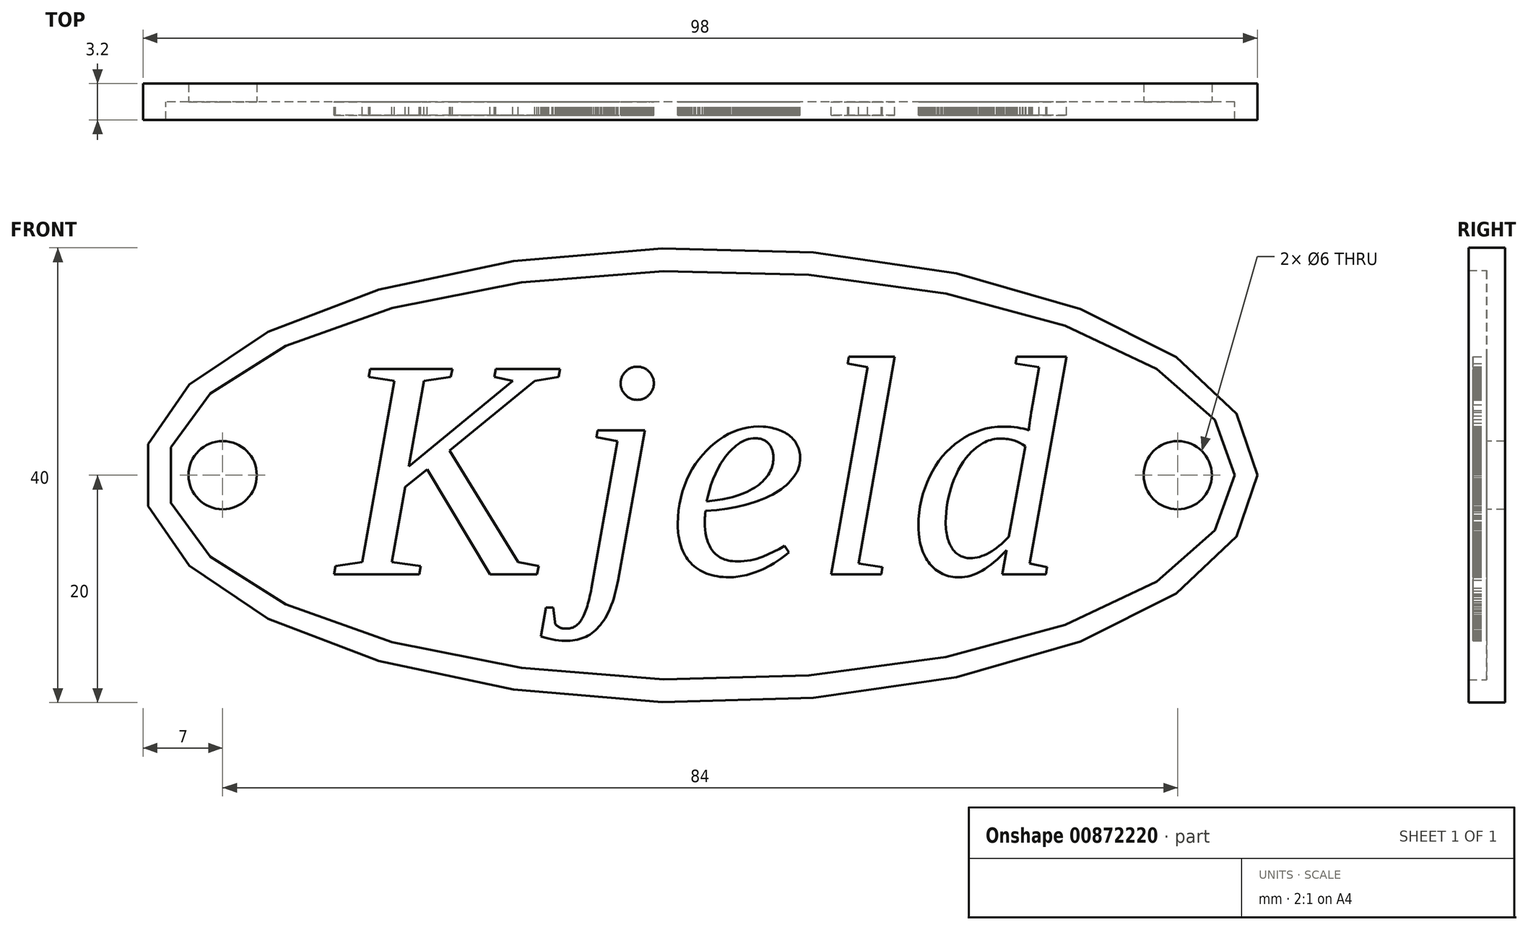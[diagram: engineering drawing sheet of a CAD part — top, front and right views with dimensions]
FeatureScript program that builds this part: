
annotation { "Feature Type Name" : "Feature", "Feature Type Description" : "" }
export const myFeature = defineFeature(function(context is Context, id is Id, definition is map)
    precondition{}
    {
        {
            var Q0;
            Q0=qCreatedBy(makeId("Front.planeOp"),FACE);
            var sketch = newSketch(context, id + "F0", { "sketchPlane" : qUnion([Q0])});
            skEllipse(sketch, "E0", {"center": v(0, 0) * mm, "majorRadius": 47 * mm, "minorRadius": 18 * mm, "majorAxis": v(1, 0)});
            skEllipse(sketch, "E1", {"center": v(0, 0) * mm, "majorRadius": 49 * mm, "minorRadius": 20 * mm, "majorAxis": v(1, 0)});
            skLineSegment(sketch, "E2", {"start": v(-81.12, 0) * mm, "end": v(85, 0) * mm, "construction": true});
            skPoint(sketch, "E2.startSnap0", {"position": v(-49, 0) * mm});
            skPoint(sketch, "E2.endSnap0", {"position": v(49, 0) * mm});
            skCircle(sketch, "E3", {"center": v(-42, 0) * mm, "radius": 3 * mm});
            skCircle(sketch, "E4", {"center": v(42, 0) * mm, "radius": 3 * mm});
            skLineSegment(sketch, "E5", {"start": v(-12.31, 9.35) * mm, "end": v(-12.45, 8.63) * mm});
            skLineSegment(sketch, "E6", {"start": v(-12.45, 8.63) * mm, "end": v(-14.55, 8.28) * mm});
            skLineSegment(sketch, "E7", {"start": v(-14.55, 8.28) * mm, "end": v(-22.03, 2.16) * mm});
            skLineSegment(sketch, "E8", {"start": v(-22.03, 2.16) * mm, "end": v(-16.02, -7.63) * mm});
            skLineSegment(sketch, "E9", {"start": v(-16.02, -7.63) * mm, "end": v(-14.21, -8) * mm});
            skLineSegment(sketch, "E10", {"start": v(-14.21, -8) * mm, "end": v(-14.35, -8.7) * mm});
            skLineSegment(sketch, "E11", {"start": v(-14.35, -8.7) * mm, "end": v(-18.48, -8.7) * mm});
            skLineSegment(sketch, "E12", {"start": v(-18.48, -8.7) * mm, "end": v(-24.01, 0.53) * mm});
            skLineSegment(sketch, "E13", {"start": v(-24.01, 0.53) * mm, "end": v(-25.94, -1.05) * mm});
            skLineSegment(sketch, "E14", {"start": v(-25.94, -1.05) * mm, "end": v(-27.12, -7.63) * mm});
            skLineSegment(sketch, "E15", {"start": v(-27.12, -7.63) * mm, "end": v(-24.6, -8) * mm});
            skLineSegment(sketch, "E16", {"start": v(-24.6, -8) * mm, "end": v(-24.73, -8.7) * mm});
            skLineSegment(sketch, "E17", {"start": v(-24.73, -8.7) * mm, "end": v(-32.21, -8.7) * mm});
            skLineSegment(sketch, "E18", {"start": v(-32.21, -8.7) * mm, "end": v(-32.08, -8) * mm});
            skLineSegment(sketch, "E19", {"start": v(-32.08, -8) * mm, "end": v(-29.72, -7.63) * mm});
            skLineSegment(sketch, "E20", {"start": v(-29.72, -7.63) * mm, "end": v(-26.9, 8.28) * mm});
            skLineSegment(sketch, "E21", {"start": v(-26.9, 8.28) * mm, "end": v(-29.17, 8.63) * mm});
            skLineSegment(sketch, "E22", {"start": v(-29.17, 8.63) * mm, "end": v(-29.03, 9.35) * mm});
            skLineSegment(sketch, "E23", {"start": v(-29.03, 9.35) * mm, "end": v(-21.8, 9.35) * mm});
            skLineSegment(sketch, "E24", {"start": v(-21.8, 9.35) * mm, "end": v(-21.94, 8.63) * mm});
            skLineSegment(sketch, "E25", {"start": v(-21.94, 8.63) * mm, "end": v(-24.3, 8.28) * mm});
            skLineSegment(sketch, "E26", {"start": v(-24.3, 8.28) * mm, "end": v(-25.63, 0.77) * mm});
            skLineSegment(sketch, "E27", {"start": v(-25.63, 0.77) * mm, "end": v(-16.5, 8.28) * mm});
            skLineSegment(sketch, "E28", {"start": v(-16.5, 8.28) * mm, "end": v(-18.1, 8.63) * mm});
            skLineSegment(sketch, "E29", {"start": v(-18.1, 8.63) * mm, "end": v(-17.97, 9.35) * mm});
            skLineSegment(sketch, "E30", {"start": v(-17.97, 9.35) * mm, "end": v(-12.31, 9.35) * mm});
            skLineSegment(sketch, "E31", {"start": v(-7.22, -9.23) * mm, "end": v(-7.36, -9.92) * mm});
            skLineSegment(sketch, "E32", {"start": v(-7.36, -9.92) * mm, "end": v(-7.52, -10.56) * mm});
            skLineSegment(sketch, "E33", {"start": v(-7.52, -10.56) * mm, "end": v(-7.61, -10.85) * mm});
            skLineSegment(sketch, "E34", {"start": v(-7.61, -10.85) * mm, "end": v(-7.7, -11.14) * mm});
            skLineSegment(sketch, "E35", {"start": v(-7.7, -11.14) * mm, "end": v(-7.8, -11.41) * mm});
            skLineSegment(sketch, "E36", {"start": v(-7.8, -11.41) * mm, "end": v(-7.9, -11.67) * mm});
            skLineSegment(sketch, "E37", {"start": v(-7.9, -11.67) * mm, "end": v(-8.02, -11.92) * mm});
            skLineSegment(sketch, "E38", {"start": v(-8.02, -11.92) * mm, "end": v(-8.13, -12.16) * mm});
            skLineSegment(sketch, "E39", {"start": v(-8.13, -12.16) * mm, "end": v(-8.25, -12.38) * mm});
            skLineSegment(sketch, "E40", {"start": v(-8.25, -12.38) * mm, "end": v(-8.37, -12.6) * mm});
            skLineSegment(sketch, "E41", {"start": v(-8.37, -12.6) * mm, "end": v(-8.5, -12.8) * mm});
            skLineSegment(sketch, "E42", {"start": v(-8.5, -12.8) * mm, "end": v(-8.63, -13) * mm});
            skLineSegment(sketch, "E43", {"start": v(-8.63, -13) * mm, "end": v(-8.77, -13.17) * mm});
            skLineSegment(sketch, "E44", {"start": v(-8.77, -13.17) * mm, "end": v(-8.92, -13.34) * mm});
            skLineSegment(sketch, "E45", {"start": v(-8.92, -13.34) * mm, "end": v(-9.07, -13.5) * mm});
            skLineSegment(sketch, "E46", {"start": v(-9.07, -13.5) * mm, "end": v(-9.22, -13.64) * mm});
            skLineSegment(sketch, "E47", {"start": v(-9.22, -13.64) * mm, "end": v(-9.38, -13.77) * mm});
            skLineSegment(sketch, "E48", {"start": v(-9.38, -13.77) * mm, "end": v(-9.54, -13.9) * mm});
            skLineSegment(sketch, "E49", {"start": v(-9.54, -13.9) * mm, "end": v(-9.7, -14.01) * mm});
            skLineSegment(sketch, "E50", {"start": v(-9.7, -14.01) * mm, "end": v(-9.88, -14.11) * mm});
            skLineSegment(sketch, "E51", {"start": v(-9.88, -14.11) * mm, "end": v(-10.06, -14.2) * mm});
            skLineSegment(sketch, "E52", {"start": v(-10.06, -14.2) * mm, "end": v(-10.24, -14.28) * mm});
            skLineSegment(sketch, "E53", {"start": v(-10.24, -14.28) * mm, "end": v(-10.43, -14.35) * mm});
            skLineSegment(sketch, "E54", {"start": v(-10.43, -14.35) * mm, "end": v(-10.62, -14.41) * mm});
            skLineSegment(sketch, "E55", {"start": v(-10.62, -14.41) * mm, "end": v(-10.81, -14.46) * mm});
            skLineSegment(sketch, "E56", {"start": v(-10.81, -14.46) * mm, "end": v(-11.01, -14.5) * mm});
            skLineSegment(sketch, "E57", {"start": v(-11.01, -14.5) * mm, "end": v(-11.22, -14.54) * mm});
            skLineSegment(sketch, "E58", {"start": v(-11.22, -14.54) * mm, "end": v(-11.43, -14.56) * mm});
            skLineSegment(sketch, "E59", {"start": v(-11.43, -14.56) * mm, "end": v(-11.64, -14.57) * mm});
            skLineSegment(sketch, "E60", {"start": v(-11.64, -14.57) * mm, "end": v(-11.85, -14.58) * mm});
            skLineSegment(sketch, "E61", {"start": v(-11.85, -14.58) * mm, "end": v(-12.16, -14.57) * mm});
            skLineSegment(sketch, "E62", {"start": v(-12.16, -14.57) * mm, "end": v(-12.45, -14.54) * mm});
            skLineSegment(sketch, "E63", {"start": v(-12.45, -14.54) * mm, "end": v(-12.75, -14.5) * mm});
            skLineSegment(sketch, "E64", {"start": v(-12.75, -14.5) * mm, "end": v(-13.04, -14.44) * mm});
            skLineSegment(sketch, "E65", {"start": v(-13.04, -14.44) * mm, "end": v(-13.32, -14.38) * mm});
            skLineSegment(sketch, "E66", {"start": v(-13.32, -14.38) * mm, "end": v(-13.45, -14.35) * mm});
            skLineSegment(sketch, "E67", {"start": v(-13.45, -14.35) * mm, "end": v(-13.57, -14.32) * mm});
            skLineSegment(sketch, "E68", {"start": v(-13.57, -14.32) * mm, "end": v(-13.69, -14.28) * mm});
            skLineSegment(sketch, "E69", {"start": v(-13.69, -14.28) * mm, "end": v(-13.8, -14.25) * mm});
            skLineSegment(sketch, "E70", {"start": v(-13.8, -14.25) * mm, "end": v(-13.9, -14.21) * mm});
            skLineSegment(sketch, "E71", {"start": v(-13.9, -14.21) * mm, "end": v(-14, -14.17) * mm});
            skLineSegment(sketch, "E72", {"start": v(-14, -14.17) * mm, "end": v(-13.56, -11.66) * mm});
            skLineSegment(sketch, "E73", {"start": v(-13.56, -11.66) * mm, "end": v(-12.93, -11.66) * mm});
            skLineSegment(sketch, "E74", {"start": v(-12.93, -11.66) * mm, "end": v(-12.73, -13.14) * mm});
            skLineSegment(sketch, "E75", {"start": v(-12.73, -13.14) * mm, "end": v(-12.7, -13.17) * mm});
            skLineSegment(sketch, "E76", {"start": v(-12.7, -13.17) * mm, "end": v(-12.65, -13.2) * mm});
            skLineSegment(sketch, "E77", {"start": v(-12.65, -13.2) * mm, "end": v(-12.6, -13.24) * mm});
            skLineSegment(sketch, "E78", {"start": v(-12.6, -13.24) * mm, "end": v(-12.56, -13.28) * mm});
            skLineSegment(sketch, "E79", {"start": v(-12.56, -13.28) * mm, "end": v(-12.51, -13.3) * mm});
            skLineSegment(sketch, "E80", {"start": v(-12.51, -13.3) * mm, "end": v(-12.46, -13.34) * mm});
            skLineSegment(sketch, "E81", {"start": v(-12.46, -13.34) * mm, "end": v(-12.4, -13.37) * mm});
            skLineSegment(sketch, "E82", {"start": v(-12.4, -13.37) * mm, "end": v(-12.35, -13.4) * mm});
            skLineSegment(sketch, "E83", {"start": v(-12.35, -13.4) * mm, "end": v(-12.3, -13.42) * mm});
            skLineSegment(sketch, "E84", {"start": v(-12.3, -13.42) * mm, "end": v(-12.23, -13.44) * mm});
            skLineSegment(sketch, "E85", {"start": v(-12.23, -13.44) * mm, "end": v(-12.16, -13.46) * mm});
            skLineSegment(sketch, "E86", {"start": v(-12.16, -13.46) * mm, "end": v(-12.1, -13.47) * mm});
            skLineSegment(sketch, "E87", {"start": v(-12.1, -13.47) * mm, "end": v(-12.02, -13.49) * mm});
            skLineSegment(sketch, "E88", {"start": v(-12.02, -13.49) * mm, "end": v(-11.94, -13.5) * mm});
            skLineSegment(sketch, "E89", {"start": v(-11.94, -13.5) * mm, "end": v(-11.86, -13.5) * mm});
            skLineSegment(sketch, "E90", {"start": v(-11.86, -13.5) * mm, "end": v(-11.77, -13.5) * mm});
            skLineSegment(sketch, "E91", {"start": v(-11.77, -13.5) * mm, "end": v(-11.68, -13.5) * mm});
            skLineSegment(sketch, "E92", {"start": v(-11.68, -13.5) * mm, "end": v(-11.59, -13.5) * mm});
            skLineSegment(sketch, "E93", {"start": v(-11.59, -13.5) * mm, "end": v(-11.5, -13.48) * mm});
            skLineSegment(sketch, "E94", {"start": v(-11.5, -13.48) * mm, "end": v(-11.41, -13.46) * mm});
            skLineSegment(sketch, "E95", {"start": v(-11.41, -13.46) * mm, "end": v(-11.32, -13.44) * mm});
            skLineSegment(sketch, "E96", {"start": v(-11.32, -13.44) * mm, "end": v(-11.24, -13.4) * mm});
            skLineSegment(sketch, "E97", {"start": v(-11.24, -13.4) * mm, "end": v(-11.16, -13.38) * mm});
            skLineSegment(sketch, "E98", {"start": v(-11.16, -13.38) * mm, "end": v(-11.07, -13.34) * mm});
            skLineSegment(sketch, "E99", {"start": v(-11.07, -13.34) * mm, "end": v(-11, -13.3) * mm});
            skLineSegment(sketch, "E100", {"start": v(-11, -13.3) * mm, "end": v(-10.92, -13.24) * mm});
            skLineSegment(sketch, "E101", {"start": v(-10.92, -13.24) * mm, "end": v(-10.84, -13.18) * mm});
            skLineSegment(sketch, "E102", {"start": v(-10.84, -13.18) * mm, "end": v(-10.76, -13.12) * mm});
            skLineSegment(sketch, "E103", {"start": v(-10.76, -13.12) * mm, "end": v(-10.7, -13.04) * mm});
            skLineSegment(sketch, "E104", {"start": v(-10.7, -13.04) * mm, "end": v(-10.62, -12.96) * mm});
            skLineSegment(sketch, "E105", {"start": v(-10.62, -12.96) * mm, "end": v(-10.55, -12.87) * mm});
            skLineSegment(sketch, "E106", {"start": v(-10.55, -12.87) * mm, "end": v(-10.48, -12.77) * mm});
            skLineSegment(sketch, "E107", {"start": v(-10.48, -12.77) * mm, "end": v(-10.41, -12.67) * mm});
            skLineSegment(sketch, "E108", {"start": v(-10.41, -12.67) * mm, "end": v(-10.35, -12.55) * mm});
            skLineSegment(sketch, "E109", {"start": v(-10.35, -12.55) * mm, "end": v(-10.29, -12.43) * mm});
            skLineSegment(sketch, "E110", {"start": v(-10.29, -12.43) * mm, "end": v(-10.22, -12.3) * mm});
            skLineSegment(sketch, "E111", {"start": v(-10.22, -12.3) * mm, "end": v(-10.16, -12.15) * mm});
            skLineSegment(sketch, "E112", {"start": v(-10.16, -12.15) * mm, "end": v(-10.1, -12) * mm});
            skLineSegment(sketch, "E113", {"start": v(-10.1, -12) * mm, "end": v(-10.04, -11.84) * mm});
            skLineSegment(sketch, "E114", {"start": v(-10.04, -11.84) * mm, "end": v(-9.98, -11.67) * mm});
            skLineSegment(sketch, "E115", {"start": v(-9.98, -11.67) * mm, "end": v(-9.93, -11.5) * mm});
            skLineSegment(sketch, "E116", {"start": v(-9.93, -11.5) * mm, "end": v(-9.87, -11.3) * mm});
            skLineSegment(sketch, "E117", {"start": v(-9.87, -11.3) * mm, "end": v(-9.82, -11.1) * mm});
            skLineSegment(sketch, "E118", {"start": v(-9.82, -11.1) * mm, "end": v(-9.76, -10.89) * mm});
            skLineSegment(sketch, "E119", {"start": v(-9.76, -10.89) * mm, "end": v(-9.71, -10.66) * mm});
            skLineSegment(sketch, "E120", {"start": v(-9.71, -10.66) * mm, "end": v(-9.66, -10.43) * mm});
            skLineSegment(sketch, "E121", {"start": v(-9.66, -10.43) * mm, "end": v(-9.61, -10.18) * mm});
            skLineSegment(sketch, "E122", {"start": v(-9.61, -10.18) * mm, "end": v(-9.57, -9.92) * mm});
            skLineSegment(sketch, "E123", {"start": v(-9.57, -9.92) * mm, "end": v(-7.28, 3) * mm});
            skLineSegment(sketch, "E124", {"start": v(-7.28, 3) * mm, "end": v(-9.12, 3.34) * mm});
            skLineSegment(sketch, "E125", {"start": v(-9.12, 3.34) * mm, "end": v(-9.01, 3.95) * mm});
            skLineSegment(sketch, "E126", {"start": v(-9.01, 3.95) * mm, "end": v(-4.88, 3.95) * mm});
            skLineSegment(sketch, "E127", {"start": v(-4.88, 3.95) * mm, "end": v(-7.22, -9.23) * mm});
            skLineSegment(sketch, "E128", {"start": v(-4.07, 8.08) * mm, "end": v(-4.07, 8) * mm});
            skLineSegment(sketch, "E129", {"start": v(-4.07, 8) * mm, "end": v(-4.08, 7.93) * mm});
            skLineSegment(sketch, "E130", {"start": v(-4.08, 7.93) * mm, "end": v(-4.1, 7.86) * mm});
            skLineSegment(sketch, "E131", {"start": v(-4.1, 7.86) * mm, "end": v(-4.1, 7.8) * mm});
            skLineSegment(sketch, "E132", {"start": v(-4.1, 7.8) * mm, "end": v(-4.12, 7.72) * mm});
            skLineSegment(sketch, "E133", {"start": v(-4.12, 7.72) * mm, "end": v(-4.14, 7.65) * mm});
            skLineSegment(sketch, "E134", {"start": v(-4.14, 7.65) * mm, "end": v(-4.17, 7.58) * mm});
            skLineSegment(sketch, "E135", {"start": v(-4.17, 7.58) * mm, "end": v(-4.2, 7.51) * mm});
            skLineSegment(sketch, "E136", {"start": v(-4.2, 7.51) * mm, "end": v(-4.22, 7.45) * mm});
            skLineSegment(sketch, "E137", {"start": v(-4.22, 7.45) * mm, "end": v(-4.25, 7.39) * mm});
            skLineSegment(sketch, "E138", {"start": v(-4.25, 7.39) * mm, "end": v(-4.29, 7.33) * mm});
            skLineSegment(sketch, "E139", {"start": v(-4.29, 7.33) * mm, "end": v(-4.33, 7.27) * mm});
            skLineSegment(sketch, "E140", {"start": v(-4.33, 7.27) * mm, "end": v(-4.37, 7.22) * mm});
            skLineSegment(sketch, "E141", {"start": v(-4.37, 7.22) * mm, "end": v(-4.4, 7.16) * mm});
            skLineSegment(sketch, "E142", {"start": v(-4.4, 7.16) * mm, "end": v(-4.45, 7.1) * mm});
            skLineSegment(sketch, "E143", {"start": v(-4.45, 7.1) * mm, "end": v(-4.5, 7.06) * mm});
            skLineSegment(sketch, "E144", {"start": v(-4.5, 7.06) * mm, "end": v(-4.56, 7) * mm});
            skLineSegment(sketch, "E145", {"start": v(-4.56, 7) * mm, "end": v(-4.6, 6.96) * mm});
            skLineSegment(sketch, "E146", {"start": v(-4.6, 6.96) * mm, "end": v(-4.66, 6.92) * mm});
            skLineSegment(sketch, "E147", {"start": v(-4.66, 6.92) * mm, "end": v(-4.72, 6.87) * mm});
            skLineSegment(sketch, "E148", {"start": v(-4.72, 6.87) * mm, "end": v(-4.78, 6.84) * mm});
            skLineSegment(sketch, "E149", {"start": v(-4.78, 6.84) * mm, "end": v(-4.84, 6.8) * mm});
            skLineSegment(sketch, "E150", {"start": v(-4.84, 6.8) * mm, "end": v(-4.9, 6.76) * mm});
            skLineSegment(sketch, "E151", {"start": v(-4.9, 6.76) * mm, "end": v(-4.98, 6.73) * mm});
            skLineSegment(sketch, "E152", {"start": v(-4.98, 6.73) * mm, "end": v(-5.04, 6.7) * mm});
            skLineSegment(sketch, "E153", {"start": v(-5.04, 6.7) * mm, "end": v(-5.11, 6.69) * mm});
            skLineSegment(sketch, "E154", {"start": v(-5.11, 6.69) * mm, "end": v(-5.18, 6.67) * mm});
            skLineSegment(sketch, "E155", {"start": v(-5.18, 6.67) * mm, "end": v(-5.25, 6.65) * mm});
            skLineSegment(sketch, "E156", {"start": v(-5.25, 6.65) * mm, "end": v(-5.32, 6.64) * mm});
            skLineSegment(sketch, "E157", {"start": v(-5.32, 6.64) * mm, "end": v(-5.4, 6.63) * mm});
            skLineSegment(sketch, "E158", {"start": v(-5.4, 6.63) * mm, "end": v(-5.47, 6.63) * mm});
            skLineSegment(sketch, "E159", {"start": v(-5.47, 6.63) * mm, "end": v(-5.54, 6.63) * mm});
            skLineSegment(sketch, "E160", {"start": v(-5.54, 6.63) * mm, "end": v(-5.61, 6.63) * mm});
            skLineSegment(sketch, "E161", {"start": v(-5.61, 6.63) * mm, "end": v(-5.69, 6.63) * mm});
            skLineSegment(sketch, "E162", {"start": v(-5.69, 6.63) * mm, "end": v(-5.76, 6.64) * mm});
            skLineSegment(sketch, "E163", {"start": v(-5.76, 6.64) * mm, "end": v(-5.83, 6.65) * mm});
            skLineSegment(sketch, "E164", {"start": v(-5.83, 6.65) * mm, "end": v(-5.9, 6.67) * mm});
            skLineSegment(sketch, "E165", {"start": v(-5.9, 6.67) * mm, "end": v(-5.97, 6.69) * mm});
            skLineSegment(sketch, "E166", {"start": v(-5.97, 6.69) * mm, "end": v(-6.04, 6.7) * mm});
            skLineSegment(sketch, "E167", {"start": v(-6.04, 6.7) * mm, "end": v(-6.1, 6.73) * mm});
            skLineSegment(sketch, "E168", {"start": v(-6.1, 6.73) * mm, "end": v(-6.23, 6.8) * mm});
            skLineSegment(sketch, "E169", {"start": v(-6.23, 6.8) * mm, "end": v(-6.35, 6.87) * mm});
            skLineSegment(sketch, "E170", {"start": v(-6.35, 6.87) * mm, "end": v(-6.46, 6.96) * mm});
            skLineSegment(sketch, "E171", {"start": v(-6.46, 6.96) * mm, "end": v(-6.56, 7.06) * mm});
            skLineSegment(sketch, "E172", {"start": v(-6.56, 7.06) * mm, "end": v(-6.66, 7.16) * mm});
            skLineSegment(sketch, "E173", {"start": v(-6.66, 7.16) * mm, "end": v(-6.75, 7.27) * mm});
            skLineSegment(sketch, "E174", {"start": v(-6.75, 7.27) * mm, "end": v(-6.82, 7.39) * mm});
            skLineSegment(sketch, "E175", {"start": v(-6.82, 7.39) * mm, "end": v(-6.89, 7.51) * mm});
            skLineSegment(sketch, "E176", {"start": v(-6.89, 7.51) * mm, "end": v(-6.91, 7.58) * mm});
            skLineSegment(sketch, "E177", {"start": v(-6.91, 7.58) * mm, "end": v(-6.93, 7.65) * mm});
            skLineSegment(sketch, "E178", {"start": v(-6.93, 7.65) * mm, "end": v(-6.95, 7.72) * mm});
            skLineSegment(sketch, "E179", {"start": v(-6.95, 7.72) * mm, "end": v(-6.97, 7.8) * mm});
            skLineSegment(sketch, "E180", {"start": v(-6.97, 7.8) * mm, "end": v(-6.98, 7.86) * mm});
            skLineSegment(sketch, "E181", {"start": v(-6.98, 7.86) * mm, "end": v(-6.99, 7.93) * mm});
            skLineSegment(sketch, "E182", {"start": v(-6.99, 7.93) * mm, "end": v(-7, 8) * mm});
            skLineSegment(sketch, "E183", {"start": v(-7, 8) * mm, "end": v(-7, 8.08) * mm});
            skLineSegment(sketch, "E184", {"start": v(-7, 8.08) * mm, "end": v(-7, 8.15) * mm});
            skLineSegment(sketch, "E185", {"start": v(-7, 8.15) * mm, "end": v(-6.99, 8.23) * mm});
            skLineSegment(sketch, "E186", {"start": v(-6.99, 8.23) * mm, "end": v(-6.98, 8.3) * mm});
            skLineSegment(sketch, "E187", {"start": v(-6.98, 8.3) * mm, "end": v(-6.97, 8.37) * mm});
            skLineSegment(sketch, "E188", {"start": v(-6.97, 8.37) * mm, "end": v(-6.95, 8.44) * mm});
            skLineSegment(sketch, "E189", {"start": v(-6.95, 8.44) * mm, "end": v(-6.93, 8.5) * mm});
            skLineSegment(sketch, "E190", {"start": v(-6.93, 8.5) * mm, "end": v(-6.91, 8.58) * mm});
            skLineSegment(sketch, "E191", {"start": v(-6.91, 8.58) * mm, "end": v(-6.89, 8.65) * mm});
            skLineSegment(sketch, "E192", {"start": v(-6.89, 8.65) * mm, "end": v(-6.86, 8.71) * mm});
            skLineSegment(sketch, "E193", {"start": v(-6.86, 8.71) * mm, "end": v(-6.82, 8.78) * mm});
            skLineSegment(sketch, "E194", {"start": v(-6.82, 8.78) * mm, "end": v(-6.78, 8.84) * mm});
            skLineSegment(sketch, "E195", {"start": v(-6.78, 8.84) * mm, "end": v(-6.75, 8.9) * mm});
            skLineSegment(sketch, "E196", {"start": v(-6.75, 8.9) * mm, "end": v(-6.7, 8.96) * mm});
            skLineSegment(sketch, "E197", {"start": v(-6.7, 8.96) * mm, "end": v(-6.66, 9.01) * mm});
            skLineSegment(sketch, "E198", {"start": v(-6.66, 9.01) * mm, "end": v(-6.61, 9.06) * mm});
            skLineSegment(sketch, "E199", {"start": v(-6.61, 9.06) * mm, "end": v(-6.56, 9.12) * mm});
            skLineSegment(sketch, "E200", {"start": v(-6.56, 9.12) * mm, "end": v(-6.51, 9.17) * mm});
            skLineSegment(sketch, "E201", {"start": v(-6.51, 9.17) * mm, "end": v(-6.46, 9.21) * mm});
            skLineSegment(sketch, "E202", {"start": v(-6.46, 9.21) * mm, "end": v(-6.4, 9.25) * mm});
            skLineSegment(sketch, "E203", {"start": v(-6.4, 9.25) * mm, "end": v(-6.35, 9.3) * mm});
            skLineSegment(sketch, "E204", {"start": v(-6.35, 9.3) * mm, "end": v(-6.3, 9.33) * mm});
            skLineSegment(sketch, "E205", {"start": v(-6.3, 9.33) * mm, "end": v(-6.23, 9.37) * mm});
            skLineSegment(sketch, "E206", {"start": v(-6.23, 9.37) * mm, "end": v(-6.17, 9.4) * mm});
            skLineSegment(sketch, "E207", {"start": v(-6.17, 9.4) * mm, "end": v(-6.1, 9.43) * mm});
            skLineSegment(sketch, "E208", {"start": v(-6.1, 9.43) * mm, "end": v(-6.04, 9.45) * mm});
            skLineSegment(sketch, "E209", {"start": v(-6.04, 9.45) * mm, "end": v(-5.97, 9.48) * mm});
            skLineSegment(sketch, "E210", {"start": v(-5.97, 9.48) * mm, "end": v(-5.9, 9.5) * mm});
            skLineSegment(sketch, "E211", {"start": v(-5.9, 9.5) * mm, "end": v(-5.83, 9.52) * mm});
            skLineSegment(sketch, "E212", {"start": v(-5.83, 9.52) * mm, "end": v(-5.76, 9.53) * mm});
            skLineSegment(sketch, "E213", {"start": v(-5.76, 9.53) * mm, "end": v(-5.69, 9.54) * mm});
            skLineSegment(sketch, "E214", {"start": v(-5.69, 9.54) * mm, "end": v(-5.61, 9.55) * mm});
            skLineSegment(sketch, "E215", {"start": v(-5.61, 9.55) * mm, "end": v(-5.54, 9.55) * mm});
            skLineSegment(sketch, "E216", {"start": v(-5.54, 9.55) * mm, "end": v(-5.47, 9.55) * mm});
            skLineSegment(sketch, "E217", {"start": v(-5.47, 9.55) * mm, "end": v(-5.4, 9.54) * mm});
            skLineSegment(sketch, "E218", {"start": v(-5.4, 9.54) * mm, "end": v(-5.32, 9.53) * mm});
            skLineSegment(sketch, "E219", {"start": v(-5.32, 9.53) * mm, "end": v(-5.25, 9.52) * mm});
            skLineSegment(sketch, "E220", {"start": v(-5.25, 9.52) * mm, "end": v(-5.18, 9.5) * mm});
            skLineSegment(sketch, "E221", {"start": v(-5.18, 9.5) * mm, "end": v(-5.11, 9.48) * mm});
            skLineSegment(sketch, "E222", {"start": v(-5.11, 9.48) * mm, "end": v(-5.04, 9.45) * mm});
            skLineSegment(sketch, "E223", {"start": v(-5.04, 9.45) * mm, "end": v(-4.98, 9.43) * mm});
            skLineSegment(sketch, "E224", {"start": v(-4.98, 9.43) * mm, "end": v(-4.9, 9.4) * mm});
            skLineSegment(sketch, "E225", {"start": v(-4.9, 9.4) * mm, "end": v(-4.84, 9.37) * mm});
            skLineSegment(sketch, "E226", {"start": v(-4.84, 9.37) * mm, "end": v(-4.78, 9.33) * mm});
            skLineSegment(sketch, "E227", {"start": v(-4.78, 9.33) * mm, "end": v(-4.72, 9.3) * mm});
            skLineSegment(sketch, "E228", {"start": v(-4.72, 9.3) * mm, "end": v(-4.66, 9.25) * mm});
            skLineSegment(sketch, "E229", {"start": v(-4.66, 9.25) * mm, "end": v(-4.6, 9.21) * mm});
            skLineSegment(sketch, "E230", {"start": v(-4.6, 9.21) * mm, "end": v(-4.56, 9.17) * mm});
            skLineSegment(sketch, "E231", {"start": v(-4.56, 9.17) * mm, "end": v(-4.5, 9.12) * mm});
            skLineSegment(sketch, "E232", {"start": v(-4.5, 9.12) * mm, "end": v(-4.45, 9.06) * mm});
            skLineSegment(sketch, "E233", {"start": v(-4.45, 9.06) * mm, "end": v(-4.4, 9.01) * mm});
            skLineSegment(sketch, "E234", {"start": v(-4.4, 9.01) * mm, "end": v(-4.37, 8.96) * mm});
            skLineSegment(sketch, "E235", {"start": v(-4.37, 8.96) * mm, "end": v(-4.33, 8.9) * mm});
            skLineSegment(sketch, "E236", {"start": v(-4.33, 8.9) * mm, "end": v(-4.29, 8.84) * mm});
            skLineSegment(sketch, "E237", {"start": v(-4.29, 8.84) * mm, "end": v(-4.25, 8.78) * mm});
            skLineSegment(sketch, "E238", {"start": v(-4.25, 8.78) * mm, "end": v(-4.22, 8.71) * mm});
            skLineSegment(sketch, "E239", {"start": v(-4.22, 8.71) * mm, "end": v(-4.2, 8.65) * mm});
            skLineSegment(sketch, "E240", {"start": v(-4.2, 8.65) * mm, "end": v(-4.17, 8.58) * mm});
            skLineSegment(sketch, "E241", {"start": v(-4.17, 8.58) * mm, "end": v(-4.14, 8.5) * mm});
            skLineSegment(sketch, "E242", {"start": v(-4.14, 8.5) * mm, "end": v(-4.12, 8.44) * mm});
            skLineSegment(sketch, "E243", {"start": v(-4.12, 8.44) * mm, "end": v(-4.1, 8.37) * mm});
            skLineSegment(sketch, "E244", {"start": v(-4.1, 8.37) * mm, "end": v(-4.1, 8.3) * mm});
            skLineSegment(sketch, "E245", {"start": v(-4.1, 8.3) * mm, "end": v(-4.08, 8.23) * mm});
            skLineSegment(sketch, "E246", {"start": v(-4.08, 8.23) * mm, "end": v(-4.07, 8.15) * mm});
            skLineSegment(sketch, "E247", {"start": v(-4.07, 8.15) * mm, "end": v(-4.07, 8.08) * mm});
            skLineSegment(sketch, "E248", {"start": v(8.8, 1.52) * mm, "end": v(8.79, 1.3) * mm});
            skLineSegment(sketch, "E249", {"start": v(8.79, 1.3) * mm, "end": v(8.76, 1.1) * mm});
            skLineSegment(sketch, "E250", {"start": v(8.76, 1.1) * mm, "end": v(8.72, 0.88) * mm});
            skLineSegment(sketch, "E251", {"start": v(8.72, 0.88) * mm, "end": v(8.66, 0.67) * mm});
            skLineSegment(sketch, "E252", {"start": v(8.66, 0.67) * mm, "end": v(8.58, 0.47) * mm});
            skLineSegment(sketch, "E253", {"start": v(8.58, 0.47) * mm, "end": v(8.49, 0.26) * mm});
            skLineSegment(sketch, "E254", {"start": v(8.49, 0.26) * mm, "end": v(8.38, 0.06) * mm});
            skLineSegment(sketch, "E255", {"start": v(8.38, 0.06) * mm, "end": v(8.25, -0.13) * mm});
            skLineSegment(sketch, "E256", {"start": v(8.25, -0.13) * mm, "end": v(8.1, -0.33) * mm});
            skLineSegment(sketch, "E257", {"start": v(8.1, -0.33) * mm, "end": v(7.94, -0.51) * mm});
            skLineSegment(sketch, "E258", {"start": v(7.94, -0.51) * mm, "end": v(7.76, -0.7) * mm});
            skLineSegment(sketch, "E259", {"start": v(7.76, -0.7) * mm, "end": v(7.57, -0.88) * mm});
            skLineSegment(sketch, "E260", {"start": v(7.57, -0.88) * mm, "end": v(7.36, -1.05) * mm});
            skLineSegment(sketch, "E261", {"start": v(7.36, -1.05) * mm, "end": v(7.13, -1.22) * mm});
            skLineSegment(sketch, "E262", {"start": v(7.13, -1.22) * mm, "end": v(6.89, -1.39) * mm});
            skLineSegment(sketch, "E263", {"start": v(6.89, -1.39) * mm, "end": v(6.63, -1.55) * mm});
            skLineSegment(sketch, "E264", {"start": v(6.63, -1.55) * mm, "end": v(6.36, -1.7) * mm});
            skLineSegment(sketch, "E265", {"start": v(6.36, -1.7) * mm, "end": v(6.07, -1.84) * mm});
            skLineSegment(sketch, "E266", {"start": v(6.07, -1.84) * mm, "end": v(5.77, -1.98) * mm});
            skLineSegment(sketch, "E267", {"start": v(5.77, -1.98) * mm, "end": v(5.45, -2.12) * mm});
            skLineSegment(sketch, "E268", {"start": v(5.45, -2.12) * mm, "end": v(5.12, -2.25) * mm});
            skLineSegment(sketch, "E269", {"start": v(5.12, -2.25) * mm, "end": v(4.77, -2.37) * mm});
            skLineSegment(sketch, "E270", {"start": v(4.77, -2.37) * mm, "end": v(4.02, -2.6) * mm});
            skLineSegment(sketch, "E271", {"start": v(4.02, -2.6) * mm, "end": v(3.22, -2.79) * mm});
            skLineSegment(sketch, "E272", {"start": v(3.22, -2.79) * mm, "end": v(2.36, -2.94) * mm});
            skLineSegment(sketch, "E273", {"start": v(2.36, -2.94) * mm, "end": v(1.44, -3.06) * mm});
            skLineSegment(sketch, "E274", {"start": v(1.44, -3.06) * mm, "end": v(0.46, -3.15) * mm});
            skLineSegment(sketch, "E275", {"start": v(0.46, -3.15) * mm, "end": v(0.46, -3.16) * mm});
            skLineSegment(sketch, "E276", {"start": v(0.46, -3.16) * mm, "end": v(0.46, -3.18) * mm});
            skLineSegment(sketch, "E277", {"start": v(0.46, -3.18) * mm, "end": v(0.46, -3.2) * mm});
            skLineSegment(sketch, "E278", {"start": v(0.46, -3.2) * mm, "end": v(0.46, -3.22) * mm});
            skLineSegment(sketch, "E279", {"start": v(0.46, -3.22) * mm, "end": v(0.45, -3.24) * mm});
            skLineSegment(sketch, "E280", {"start": v(0.45, -3.24) * mm, "end": v(0.45, -3.26) * mm});
            skLineSegment(sketch, "E281", {"start": v(0.45, -3.26) * mm, "end": v(0.45, -3.28) * mm});
            skLineSegment(sketch, "E282", {"start": v(0.45, -3.28) * mm, "end": v(0.45, -3.3) * mm});
            skLineSegment(sketch, "E283", {"start": v(0.45, -3.3) * mm, "end": v(0.44, -3.35) * mm});
            skLineSegment(sketch, "E284", {"start": v(0.44, -3.35) * mm, "end": v(0.44, -3.4) * mm});
            skLineSegment(sketch, "E285", {"start": v(0.44, -3.4) * mm, "end": v(0.43, -3.46) * mm});
            skLineSegment(sketch, "E286", {"start": v(0.43, -3.46) * mm, "end": v(0.42, -3.53) * mm});
            skLineSegment(sketch, "E287", {"start": v(0.42, -3.53) * mm, "end": v(0.42, -3.6) * mm});
            skLineSegment(sketch, "E288", {"start": v(0.42, -3.6) * mm, "end": v(0.42, -3.73) * mm});
            skLineSegment(sketch, "E289", {"start": v(0.42, -3.73) * mm, "end": v(0.41, -3.88) * mm});
            skLineSegment(sketch, "E290", {"start": v(0.41, -3.88) * mm, "end": v(0.41, -4.04) * mm});
            skLineSegment(sketch, "E291", {"start": v(0.41, -4.04) * mm, "end": v(0.41, -4.13) * mm});
            skLineSegment(sketch, "E292", {"start": v(0.41, -4.13) * mm, "end": v(0.42, -4.46) * mm});
            skLineSegment(sketch, "E293", {"start": v(0.42, -4.46) * mm, "end": v(0.44, -4.78) * mm});
            skLineSegment(sketch, "E294", {"start": v(0.44, -4.78) * mm, "end": v(0.48, -5.1) * mm});
            skLineSegment(sketch, "E295", {"start": v(0.48, -5.1) * mm, "end": v(0.53, -5.4) * mm});
            skLineSegment(sketch, "E296", {"start": v(0.53, -5.4) * mm, "end": v(0.57, -5.56) * mm});
            skLineSegment(sketch, "E297", {"start": v(0.57, -5.56) * mm, "end": v(0.61, -5.71) * mm});
            skLineSegment(sketch, "E298", {"start": v(0.61, -5.71) * mm, "end": v(0.66, -5.86) * mm});
            skLineSegment(sketch, "E299", {"start": v(0.66, -5.86) * mm, "end": v(0.71, -6) * mm});
            skLineSegment(sketch, "E300", {"start": v(0.71, -6) * mm, "end": v(0.77, -6.13) * mm});
            skLineSegment(sketch, "E301", {"start": v(0.77, -6.13) * mm, "end": v(0.84, -6.26) * mm});
            skLineSegment(sketch, "E302", {"start": v(0.84, -6.26) * mm, "end": v(0.91, -6.4) * mm});
            skLineSegment(sketch, "E303", {"start": v(0.91, -6.4) * mm, "end": v(0.99, -6.51) * mm});
            skLineSegment(sketch, "E304", {"start": v(0.99, -6.51) * mm, "end": v(1.07, -6.63) * mm});
            skLineSegment(sketch, "E305", {"start": v(1.07, -6.63) * mm, "end": v(1.17, -6.74) * mm});
            skLineSegment(sketch, "E306", {"start": v(1.17, -6.74) * mm, "end": v(1.26, -6.85) * mm});
            skLineSegment(sketch, "E307", {"start": v(1.26, -6.85) * mm, "end": v(1.37, -6.95) * mm});
            skLineSegment(sketch, "E308", {"start": v(1.37, -6.95) * mm, "end": v(1.48, -7.05) * mm});
            skLineSegment(sketch, "E309", {"start": v(1.48, -7.05) * mm, "end": v(1.6, -7.13) * mm});
            skLineSegment(sketch, "E310", {"start": v(1.6, -7.13) * mm, "end": v(1.73, -7.22) * mm});
            skLineSegment(sketch, "E311", {"start": v(1.73, -7.22) * mm, "end": v(1.86, -7.3) * mm});
            skLineSegment(sketch, "E312", {"start": v(1.86, -7.3) * mm, "end": v(2, -7.36) * mm});
            skLineSegment(sketch, "E313", {"start": v(2, -7.36) * mm, "end": v(2.16, -7.42) * mm});
            skLineSegment(sketch, "E314", {"start": v(2.16, -7.42) * mm, "end": v(2.32, -7.47) * mm});
            skLineSegment(sketch, "E315", {"start": v(2.32, -7.47) * mm, "end": v(2.5, -7.5) * mm});
            skLineSegment(sketch, "E316", {"start": v(2.5, -7.5) * mm, "end": v(2.67, -7.54) * mm});
            skLineSegment(sketch, "E317", {"start": v(2.67, -7.54) * mm, "end": v(2.86, -7.56) * mm});
            skLineSegment(sketch, "E318", {"start": v(2.86, -7.56) * mm, "end": v(3.06, -7.57) * mm});
            skLineSegment(sketch, "E319", {"start": v(3.06, -7.57) * mm, "end": v(3.26, -7.58) * mm});
            skLineSegment(sketch, "E320", {"start": v(3.26, -7.58) * mm, "end": v(3.56, -7.57) * mm});
            skLineSegment(sketch, "E321", {"start": v(3.56, -7.57) * mm, "end": v(3.86, -7.55) * mm});
            skLineSegment(sketch, "E322", {"start": v(3.86, -7.55) * mm, "end": v(4.15, -7.52) * mm});
            skLineSegment(sketch, "E323", {"start": v(4.15, -7.52) * mm, "end": v(4.43, -7.48) * mm});
            skLineSegment(sketch, "E324", {"start": v(4.43, -7.48) * mm, "end": v(4.7, -7.42) * mm});
            skLineSegment(sketch, "E325", {"start": v(4.7, -7.42) * mm, "end": v(4.98, -7.35) * mm});
            skLineSegment(sketch, "E326", {"start": v(4.98, -7.35) * mm, "end": v(5.24, -7.27) * mm});
            skLineSegment(sketch, "E327", {"start": v(5.24, -7.27) * mm, "end": v(5.5, -7.17) * mm});
            skLineSegment(sketch, "E328", {"start": v(5.5, -7.17) * mm, "end": v(6, -6.96) * mm});
            skLineSegment(sketch, "E329", {"start": v(6, -6.96) * mm, "end": v(6.96, -6.49) * mm});
            skLineSegment(sketch, "E330", {"start": v(6.96, -6.49) * mm, "end": v(7.41, -6.23) * mm});
            skLineSegment(sketch, "E331", {"start": v(7.41, -6.23) * mm, "end": v(7.8, -6.8) * mm});
            skLineSegment(sketch, "E332", {"start": v(7.8, -6.8) * mm, "end": v(7.58, -6.98) * mm});
            skLineSegment(sketch, "E333", {"start": v(7.58, -6.98) * mm, "end": v(7.33, -7.17) * mm});
            skLineSegment(sketch, "E334", {"start": v(7.33, -7.17) * mm, "end": v(7.07, -7.36) * mm});
            skLineSegment(sketch, "E335", {"start": v(7.07, -7.36) * mm, "end": v(6.8, -7.55) * mm});
            skLineSegment(sketch, "E336", {"start": v(6.8, -7.55) * mm, "end": v(6.5, -7.74) * mm});
            skLineSegment(sketch, "E337", {"start": v(6.5, -7.74) * mm, "end": v(6.19, -7.92) * mm});
            skLineSegment(sketch, "E338", {"start": v(6.19, -7.92) * mm, "end": v(5.53, -8.26) * mm});
            skLineSegment(sketch, "E339", {"start": v(5.53, -8.26) * mm, "end": v(5.18, -8.41) * mm});
            skLineSegment(sketch, "E340", {"start": v(5.18, -8.41) * mm, "end": v(4.83, -8.55) * mm});
            skLineSegment(sketch, "E341", {"start": v(4.83, -8.55) * mm, "end": v(4.47, -8.67) * mm});
            skLineSegment(sketch, "E342", {"start": v(4.47, -8.67) * mm, "end": v(4.1, -8.78) * mm});
            skLineSegment(sketch, "E343", {"start": v(4.1, -8.78) * mm, "end": v(3.72, -8.86) * mm});
            skLineSegment(sketch, "E344", {"start": v(3.72, -8.86) * mm, "end": v(3.34, -8.93) * mm});
            skLineSegment(sketch, "E345", {"start": v(3.34, -8.93) * mm, "end": v(2.95, -8.96) * mm});
            skLineSegment(sketch, "E346", {"start": v(2.95, -8.96) * mm, "end": v(2.56, -8.98) * mm});
            skLineSegment(sketch, "E347", {"start": v(2.56, -8.98) * mm, "end": v(2.28, -8.97) * mm});
            skLineSegment(sketch, "E348", {"start": v(2.28, -8.97) * mm, "end": v(2.01, -8.96) * mm});
            skLineSegment(sketch, "E349", {"start": v(2.01, -8.96) * mm, "end": v(1.75, -8.93) * mm});
            skLineSegment(sketch, "E350", {"start": v(1.75, -8.93) * mm, "end": v(1.5, -8.9) * mm});
            skLineSegment(sketch, "E351", {"start": v(1.5, -8.9) * mm, "end": v(1.25, -8.85) * mm});
            skLineSegment(sketch, "E352", {"start": v(1.25, -8.85) * mm, "end": v(1.01, -8.8) * mm});
            skLineSegment(sketch, "E353", {"start": v(1.01, -8.8) * mm, "end": v(0.79, -8.73) * mm});
            skLineSegment(sketch, "E354", {"start": v(0.79, -8.73) * mm, "end": v(0.57, -8.65) * mm});
            skLineSegment(sketch, "E355", {"start": v(0.57, -8.65) * mm, "end": v(0.36, -8.57) * mm});
            skLineSegment(sketch, "E356", {"start": v(0.36, -8.57) * mm, "end": v(0.17, -8.47) * mm});
            skLineSegment(sketch, "E357", {"start": v(0.17, -8.47) * mm, "end": v(-0.02, -8.36) * mm});
            skLineSegment(sketch, "E358", {"start": v(-0.02, -8.36) * mm, "end": v(-0.2, -8.25) * mm});
            skLineSegment(sketch, "E359", {"start": v(-0.2, -8.25) * mm, "end": v(-0.38, -8.13) * mm});
            skLineSegment(sketch, "E360", {"start": v(-0.38, -8.13) * mm, "end": v(-0.54, -8) * mm});
            skLineSegment(sketch, "E361", {"start": v(-0.54, -8) * mm, "end": v(-0.7, -7.86) * mm});
            skLineSegment(sketch, "E362", {"start": v(-0.7, -7.86) * mm, "end": v(-0.84, -7.71) * mm});
            skLineSegment(sketch, "E363", {"start": v(-0.84, -7.71) * mm, "end": v(-0.98, -7.56) * mm});
            skLineSegment(sketch, "E364", {"start": v(-0.98, -7.56) * mm, "end": v(-1.1, -7.4) * mm});
            skLineSegment(sketch, "E365", {"start": v(-1.1, -7.4) * mm, "end": v(-1.23, -7.22) * mm});
            skLineSegment(sketch, "E366", {"start": v(-1.23, -7.22) * mm, "end": v(-1.34, -7.04) * mm});
            skLineSegment(sketch, "E367", {"start": v(-1.34, -7.04) * mm, "end": v(-1.44, -6.85) * mm});
            skLineSegment(sketch, "E368", {"start": v(-1.44, -6.85) * mm, "end": v(-1.53, -6.65) * mm});
            skLineSegment(sketch, "E369", {"start": v(-1.53, -6.65) * mm, "end": v(-1.61, -6.45) * mm});
            skLineSegment(sketch, "E370", {"start": v(-1.61, -6.45) * mm, "end": v(-1.69, -6.23) * mm});
            skLineSegment(sketch, "E371", {"start": v(-1.69, -6.23) * mm, "end": v(-1.76, -6) * mm});
            skLineSegment(sketch, "E372", {"start": v(-1.76, -6) * mm, "end": v(-1.81, -5.78) * mm});
            skLineSegment(sketch, "E373", {"start": v(-1.81, -5.78) * mm, "end": v(-1.86, -5.54) * mm});
            skLineSegment(sketch, "E374", {"start": v(-1.86, -5.54) * mm, "end": v(-1.9, -5.3) * mm});
            skLineSegment(sketch, "E375", {"start": v(-1.9, -5.3) * mm, "end": v(-1.93, -5.05) * mm});
            skLineSegment(sketch, "E376", {"start": v(-1.93, -5.05) * mm, "end": v(-1.97, -4.53) * mm});
            skLineSegment(sketch, "E377", {"start": v(-1.97, -4.53) * mm, "end": v(-1.97, -4.27) * mm});
            skLineSegment(sketch, "E378", {"start": v(-1.97, -4.27) * mm, "end": v(-1.96, -3.67) * mm});
            skLineSegment(sketch, "E379", {"start": v(-1.96, -3.67) * mm, "end": v(-1.9, -3.1) * mm});
            skLineSegment(sketch, "E380", {"start": v(-1.9, -3.1) * mm, "end": v(-1.82, -2.53) * mm});
            skLineSegment(sketch, "E381", {"start": v(-1.82, -2.53) * mm, "end": v(-1.7, -1.98) * mm});
            skLineSegment(sketch, "E382", {"start": v(-1.7, -1.98) * mm, "end": v(-1.55, -1.43) * mm});
            skLineSegment(sketch, "E383", {"start": v(-1.55, -1.43) * mm, "end": v(-1.38, -0.91) * mm});
            skLineSegment(sketch, "E384", {"start": v(-1.38, -0.91) * mm, "end": v(-1.18, -0.41) * mm});
            skLineSegment(sketch, "E385", {"start": v(-1.18, -0.41) * mm, "end": v(-0.95, 0.07) * mm});
            skLineSegment(sketch, "E386", {"start": v(-0.95, 0.07) * mm, "end": v(-0.7, 0.54) * mm});
            skLineSegment(sketch, "E387", {"start": v(-0.7, 0.54) * mm, "end": v(-0.42, 0.98) * mm});
            skLineSegment(sketch, "E388", {"start": v(-0.42, 0.98) * mm, "end": v(-0.12, 1.4) * mm});
            skLineSegment(sketch, "E389", {"start": v(-0.12, 1.4) * mm, "end": v(0.2, 1.8) * mm});
            skLineSegment(sketch, "E390", {"start": v(0.2, 1.8) * mm, "end": v(0.55, 2.17) * mm});
            skLineSegment(sketch, "E391", {"start": v(0.55, 2.17) * mm, "end": v(0.9, 2.52) * mm});
            skLineSegment(sketch, "E392", {"start": v(0.9, 2.52) * mm, "end": v(1.28, 2.84) * mm});
            skLineSegment(sketch, "E393", {"start": v(1.28, 2.84) * mm, "end": v(1.66, 3.13) * mm});
            skLineSegment(sketch, "E394", {"start": v(1.66, 3.13) * mm, "end": v(2.06, 3.39) * mm});
            skLineSegment(sketch, "E395", {"start": v(2.06, 3.39) * mm, "end": v(2.48, 3.61) * mm});
            skLineSegment(sketch, "E396", {"start": v(2.48, 3.61) * mm, "end": v(2.9, 3.8) * mm});
            skLineSegment(sketch, "E397", {"start": v(2.9, 3.8) * mm, "end": v(3.33, 3.97) * mm});
            skLineSegment(sketch, "E398", {"start": v(3.33, 3.97) * mm, "end": v(3.78, 4.1) * mm});
            skLineSegment(sketch, "E399", {"start": v(3.78, 4.1) * mm, "end": v(4.23, 4.2) * mm});
            skLineSegment(sketch, "E400", {"start": v(4.23, 4.2) * mm, "end": v(4.68, 4.26) * mm});
            skLineSegment(sketch, "E401", {"start": v(4.68, 4.26) * mm, "end": v(5.14, 4.28) * mm});
            skLineSegment(sketch, "E402", {"start": v(5.14, 4.28) * mm, "end": v(5.55, 4.27) * mm});
            skLineSegment(sketch, "E403", {"start": v(5.55, 4.27) * mm, "end": v(5.76, 4.25) * mm});
            skLineSegment(sketch, "E404", {"start": v(5.76, 4.25) * mm, "end": v(5.95, 4.23) * mm});
            skLineSegment(sketch, "E405", {"start": v(5.95, 4.23) * mm, "end": v(6.14, 4.2) * mm});
            skLineSegment(sketch, "E406", {"start": v(6.14, 4.2) * mm, "end": v(6.32, 4.16) * mm});
            skLineSegment(sketch, "E407", {"start": v(6.32, 4.16) * mm, "end": v(6.5, 4.12) * mm});
            skLineSegment(sketch, "E408", {"start": v(6.5, 4.12) * mm, "end": v(6.67, 4.07) * mm});
            skLineSegment(sketch, "E409", {"start": v(6.67, 4.07) * mm, "end": v(6.84, 4.01) * mm});
            skLineSegment(sketch, "E410", {"start": v(6.84, 4.01) * mm, "end": v(7, 3.96) * mm});
            skLineSegment(sketch, "E411", {"start": v(7, 3.96) * mm, "end": v(7.16, 3.9) * mm});
            skLineSegment(sketch, "E412", {"start": v(7.16, 3.9) * mm, "end": v(7.3, 3.82) * mm});
            skLineSegment(sketch, "E413", {"start": v(7.3, 3.82) * mm, "end": v(7.44, 3.75) * mm});
            skLineSegment(sketch, "E414", {"start": v(7.44, 3.75) * mm, "end": v(7.58, 3.67) * mm});
            skLineSegment(sketch, "E415", {"start": v(7.58, 3.67) * mm, "end": v(7.7, 3.58) * mm});
            skLineSegment(sketch, "E416", {"start": v(7.7, 3.58) * mm, "end": v(7.83, 3.49) * mm});
            skLineSegment(sketch, "E417", {"start": v(7.83, 3.49) * mm, "end": v(7.94, 3.4) * mm});
            skLineSegment(sketch, "E418", {"start": v(7.94, 3.4) * mm, "end": v(8.05, 3.3) * mm});
            skLineSegment(sketch, "E419", {"start": v(8.05, 3.3) * mm, "end": v(8.15, 3.2) * mm});
            skLineSegment(sketch, "E420", {"start": v(8.15, 3.2) * mm, "end": v(8.24, 3.09) * mm});
            skLineSegment(sketch, "E421", {"start": v(8.24, 3.09) * mm, "end": v(8.33, 2.98) * mm});
            skLineSegment(sketch, "E422", {"start": v(8.33, 2.98) * mm, "end": v(8.4, 2.86) * mm});
            skLineSegment(sketch, "E423", {"start": v(8.4, 2.86) * mm, "end": v(8.48, 2.74) * mm});
            skLineSegment(sketch, "E424", {"start": v(8.48, 2.74) * mm, "end": v(8.54, 2.61) * mm});
            skLineSegment(sketch, "E425", {"start": v(8.54, 2.61) * mm, "end": v(8.6, 2.49) * mm});
            skLineSegment(sketch, "E426", {"start": v(8.6, 2.49) * mm, "end": v(8.65, 2.36) * mm});
            skLineSegment(sketch, "E427", {"start": v(8.65, 2.36) * mm, "end": v(8.7, 2.23) * mm});
            skLineSegment(sketch, "E428", {"start": v(8.7, 2.23) * mm, "end": v(8.73, 2.1) * mm});
            skLineSegment(sketch, "E429", {"start": v(8.73, 2.1) * mm, "end": v(8.76, 1.95) * mm});
            skLineSegment(sketch, "E430", {"start": v(8.76, 1.95) * mm, "end": v(8.78, 1.81) * mm});
            skLineSegment(sketch, "E431", {"start": v(8.78, 1.81) * mm, "end": v(8.8, 1.67) * mm});
            skLineSegment(sketch, "E432", {"start": v(8.8, 1.67) * mm, "end": v(8.8, 1.52) * mm});
            skLineSegment(sketch, "E433", {"start": v(0.57, -2.3) * mm, "end": v(1.28, -2.23) * mm});
            skLineSegment(sketch, "E434", {"start": v(1.28, -2.23) * mm, "end": v(1.95, -2.13) * mm});
            skLineSegment(sketch, "E435", {"start": v(1.95, -2.13) * mm, "end": v(2.57, -2) * mm});
            skLineSegment(sketch, "E436", {"start": v(2.57, -2) * mm, "end": v(2.86, -1.93) * mm});
            skLineSegment(sketch, "E437", {"start": v(2.86, -1.93) * mm, "end": v(3.14, -1.84) * mm});
            skLineSegment(sketch, "E438", {"start": v(3.14, -1.84) * mm, "end": v(3.41, -1.75) * mm});
            skLineSegment(sketch, "E439", {"start": v(3.41, -1.75) * mm, "end": v(3.67, -1.65) * mm});
            skLineSegment(sketch, "E440", {"start": v(3.67, -1.65) * mm, "end": v(3.92, -1.55) * mm});
            skLineSegment(sketch, "E441", {"start": v(3.92, -1.55) * mm, "end": v(4.15, -1.44) * mm});
            skLineSegment(sketch, "E442", {"start": v(4.15, -1.44) * mm, "end": v(4.38, -1.33) * mm});
            skLineSegment(sketch, "E443", {"start": v(4.38, -1.33) * mm, "end": v(4.59, -1.21) * mm});
            skLineSegment(sketch, "E444", {"start": v(4.59, -1.21) * mm, "end": v(4.79, -1.1) * mm});
            skLineSegment(sketch, "E445", {"start": v(4.79, -1.1) * mm, "end": v(4.97, -0.97) * mm});
            skLineSegment(sketch, "E446", {"start": v(4.97, -0.97) * mm, "end": v(5.15, -0.83) * mm});
            skLineSegment(sketch, "E447", {"start": v(5.15, -0.83) * mm, "end": v(5.32, -0.7) * mm});
            skLineSegment(sketch, "E448", {"start": v(5.32, -0.7) * mm, "end": v(5.48, -0.56) * mm});
            skLineSegment(sketch, "E449", {"start": v(5.48, -0.56) * mm, "end": v(5.62, -0.42) * mm});
            skLineSegment(sketch, "E450", {"start": v(5.62, -0.42) * mm, "end": v(5.75, -0.27) * mm});
            skLineSegment(sketch, "E451", {"start": v(5.75, -0.27) * mm, "end": v(5.87, -0.12) * mm});
            skLineSegment(sketch, "E452", {"start": v(5.87, -0.12) * mm, "end": v(5.98, 0.03) * mm});
            skLineSegment(sketch, "E453", {"start": v(5.98, 0.03) * mm, "end": v(6.08, 0.2) * mm});
            skLineSegment(sketch, "E454", {"start": v(6.08, 0.2) * mm, "end": v(6.16, 0.35) * mm});
            skLineSegment(sketch, "E455", {"start": v(6.16, 0.35) * mm, "end": v(6.24, 0.52) * mm});
            skLineSegment(sketch, "E456", {"start": v(6.24, 0.52) * mm, "end": v(6.3, 0.68) * mm});
            skLineSegment(sketch, "E457", {"start": v(6.3, 0.68) * mm, "end": v(6.35, 0.85) * mm});
            skLineSegment(sketch, "E458", {"start": v(6.35, 0.85) * mm, "end": v(6.4, 1.01) * mm});
            skLineSegment(sketch, "E459", {"start": v(6.4, 1.01) * mm, "end": v(6.42, 1.18) * mm});
            skLineSegment(sketch, "E460", {"start": v(6.42, 1.18) * mm, "end": v(6.44, 1.35) * mm});
            skLineSegment(sketch, "E461", {"start": v(6.44, 1.35) * mm, "end": v(6.44, 1.52) * mm});
            skLineSegment(sketch, "E462", {"start": v(6.44, 1.52) * mm, "end": v(6.44, 1.7) * mm});
            skLineSegment(sketch, "E463", {"start": v(6.44, 1.7) * mm, "end": v(6.43, 1.8) * mm});
            skLineSegment(sketch, "E464", {"start": v(6.43, 1.8) * mm, "end": v(6.42, 1.88) * mm});
            skLineSegment(sketch, "E465", {"start": v(6.42, 1.88) * mm, "end": v(6.4, 1.97) * mm});
            skLineSegment(sketch, "E466", {"start": v(6.4, 1.97) * mm, "end": v(6.38, 2.05) * mm});
            skLineSegment(sketch, "E467", {"start": v(6.38, 2.05) * mm, "end": v(6.36, 2.13) * mm});
            skLineSegment(sketch, "E468", {"start": v(6.36, 2.13) * mm, "end": v(6.34, 2.2) * mm});
            skLineSegment(sketch, "E469", {"start": v(6.34, 2.2) * mm, "end": v(6.3, 2.29) * mm});
            skLineSegment(sketch, "E470", {"start": v(6.3, 2.29) * mm, "end": v(6.28, 2.36) * mm});
            skLineSegment(sketch, "E471", {"start": v(6.28, 2.36) * mm, "end": v(6.24, 2.43) * mm});
            skLineSegment(sketch, "E472", {"start": v(6.24, 2.43) * mm, "end": v(6.2, 2.5) * mm});
            skLineSegment(sketch, "E473", {"start": v(6.2, 2.5) * mm, "end": v(6.17, 2.57) * mm});
            skLineSegment(sketch, "E474", {"start": v(6.17, 2.57) * mm, "end": v(6.12, 2.64) * mm});
            skLineSegment(sketch, "E475", {"start": v(6.12, 2.64) * mm, "end": v(6.08, 2.7) * mm});
            skLineSegment(sketch, "E476", {"start": v(6.08, 2.7) * mm, "end": v(6.02, 2.76) * mm});
            skLineSegment(sketch, "E477", {"start": v(6.02, 2.76) * mm, "end": v(5.97, 2.82) * mm});
            skLineSegment(sketch, "E478", {"start": v(5.97, 2.82) * mm, "end": v(5.92, 2.88) * mm});
            skLineSegment(sketch, "E479", {"start": v(5.92, 2.88) * mm, "end": v(5.86, 2.93) * mm});
            skLineSegment(sketch, "E480", {"start": v(5.86, 2.93) * mm, "end": v(5.8, 2.97) * mm});
            skLineSegment(sketch, "E481", {"start": v(5.8, 2.97) * mm, "end": v(5.74, 3.02) * mm});
            skLineSegment(sketch, "E482", {"start": v(5.74, 3.02) * mm, "end": v(5.67, 3.06) * mm});
            skLineSegment(sketch, "E483", {"start": v(5.67, 3.06) * mm, "end": v(5.6, 3.1) * mm});
            skLineSegment(sketch, "E484", {"start": v(5.6, 3.1) * mm, "end": v(5.53, 3.13) * mm});
            skLineSegment(sketch, "E485", {"start": v(5.53, 3.13) * mm, "end": v(5.45, 3.15) * mm});
            skLineSegment(sketch, "E486", {"start": v(5.45, 3.15) * mm, "end": v(5.37, 3.18) * mm});
            skLineSegment(sketch, "E487", {"start": v(5.37, 3.18) * mm, "end": v(5.3, 3.2) * mm});
            skLineSegment(sketch, "E488", {"start": v(5.3, 3.2) * mm, "end": v(5.2, 3.22) * mm});
            skLineSegment(sketch, "E489", {"start": v(5.2, 3.22) * mm, "end": v(5.12, 3.23) * mm});
            skLineSegment(sketch, "E490", {"start": v(5.12, 3.23) * mm, "end": v(5.03, 3.24) * mm});
            skLineSegment(sketch, "E491", {"start": v(5.03, 3.24) * mm, "end": v(4.94, 3.24) * mm});
            skLineSegment(sketch, "E492", {"start": v(4.94, 3.24) * mm, "end": v(4.84, 3.25) * mm});
            skLineSegment(sketch, "E493", {"start": v(4.84, 3.25) * mm, "end": v(4.64, 3.24) * mm});
            skLineSegment(sketch, "E494", {"start": v(4.64, 3.24) * mm, "end": v(4.45, 3.21) * mm});
            skLineSegment(sketch, "E495", {"start": v(4.45, 3.21) * mm, "end": v(4.26, 3.17) * mm});
            skLineSegment(sketch, "E496", {"start": v(4.26, 3.17) * mm, "end": v(4.07, 3.12) * mm});
            skLineSegment(sketch, "E497", {"start": v(4.07, 3.12) * mm, "end": v(3.88, 3.05) * mm});
            skLineSegment(sketch, "E498", {"start": v(3.88, 3.05) * mm, "end": v(3.7, 2.96) * mm});
            skLineSegment(sketch, "E499", {"start": v(3.7, 2.96) * mm, "end": v(3.52, 2.85) * mm});
            skLineSegment(sketch, "E500", {"start": v(3.52, 2.85) * mm, "end": v(3.35, 2.74) * mm});
            skLineSegment(sketch, "E501", {"start": v(3.35, 2.74) * mm, "end": v(3.17, 2.6) * mm});
            skLineSegment(sketch, "E502", {"start": v(3.17, 2.6) * mm, "end": v(3, 2.47) * mm});
            skLineSegment(sketch, "E503", {"start": v(3, 2.47) * mm, "end": v(2.84, 2.32) * mm});
            skLineSegment(sketch, "E504", {"start": v(2.84, 2.32) * mm, "end": v(2.68, 2.16) * mm});
            skLineSegment(sketch, "E505", {"start": v(2.68, 2.16) * mm, "end": v(2.52, 2) * mm});
            skLineSegment(sketch, "E506", {"start": v(2.52, 2) * mm, "end": v(2.22, 1.64) * mm});
            skLineSegment(sketch, "E507", {"start": v(2.22, 1.64) * mm, "end": v(2.08, 1.44) * mm});
            skLineSegment(sketch, "E508", {"start": v(2.08, 1.44) * mm, "end": v(1.81, 1.03) * mm});
            skLineSegment(sketch, "E509", {"start": v(1.81, 1.03) * mm, "end": v(1.57, 0.6) * mm});
            skLineSegment(sketch, "E510", {"start": v(1.57, 0.6) * mm, "end": v(1.34, 0.14) * mm});
            skLineSegment(sketch, "E511", {"start": v(1.34, 0.14) * mm, "end": v(1.14, -0.35) * mm});
            skLineSegment(sketch, "E512", {"start": v(1.14, -0.35) * mm, "end": v(0.96, -0.84) * mm});
            skLineSegment(sketch, "E513", {"start": v(0.96, -0.84) * mm, "end": v(0.8, -1.33) * mm});
            skLineSegment(sketch, "E514", {"start": v(0.8, -1.33) * mm, "end": v(0.67, -1.81) * mm});
            skLineSegment(sketch, "E515", {"start": v(0.67, -1.81) * mm, "end": v(0.57, -2.3) * mm});
            skLineSegment(sketch, "E516", {"start": v(13.91, -7.77) * mm, "end": v(16.03, -8.1) * mm});
            skLineSegment(sketch, "E517", {"start": v(16.03, -8.1) * mm, "end": v(15.92, -8.7) * mm});
            skLineSegment(sketch, "E518", {"start": v(15.92, -8.7) * mm, "end": v(11.52, -8.7) * mm});
            skLineSegment(sketch, "E519", {"start": v(11.52, -8.7) * mm, "end": v(14.7, 9.5) * mm});
            skLineSegment(sketch, "E520", {"start": v(14.7, 9.5) * mm, "end": v(12.97, 9.82) * mm});
            skLineSegment(sketch, "E521", {"start": v(12.97, 9.82) * mm, "end": v(13.08, 10.42) * mm});
            skLineSegment(sketch, "E522", {"start": v(13.08, 10.42) * mm, "end": v(17.1, 10.42) * mm});
            skLineSegment(sketch, "E523", {"start": v(17.1, 10.42) * mm, "end": v(13.91, -7.77) * mm});
            skLineSegment(sketch, "E524", {"start": v(28.9, 3.96) * mm, "end": v(28.9, 3.98) * mm});
            skLineSegment(sketch, "E525", {"start": v(28.9, 3.98) * mm, "end": v(28.9, 4) * mm});
            skLineSegment(sketch, "E526", {"start": v(28.9, 4) * mm, "end": v(28.9, 4.03) * mm});
            skLineSegment(sketch, "E527", {"start": v(28.9, 4.03) * mm, "end": v(28.9, 4.05) * mm});
            skLineSegment(sketch, "E528", {"start": v(28.9, 4.05) * mm, "end": v(28.91, 4.1) * mm});
            skLineSegment(sketch, "E529", {"start": v(28.91, 4.1) * mm, "end": v(28.92, 4.16) * mm});
            skLineSegment(sketch, "E530", {"start": v(28.92, 4.16) * mm, "end": v(28.93, 4.21) * mm});
            skLineSegment(sketch, "E531", {"start": v(28.93, 4.21) * mm, "end": v(28.93, 4.28) * mm});
            skLineSegment(sketch, "E532", {"start": v(28.93, 4.28) * mm, "end": v(28.94, 4.35) * mm});
            skLineSegment(sketch, "E533", {"start": v(28.94, 4.35) * mm, "end": v(28.95, 4.42) * mm});
            skLineSegment(sketch, "E534", {"start": v(28.95, 4.42) * mm, "end": v(28.97, 4.57) * mm});
            skLineSegment(sketch, "E535", {"start": v(28.97, 4.57) * mm, "end": v(29.02, 4.89) * mm});
            skLineSegment(sketch, "E536", {"start": v(29.02, 4.89) * mm, "end": v(29.05, 5.05) * mm});
            skLineSegment(sketch, "E537", {"start": v(29.05, 5.05) * mm, "end": v(29.07, 5.22) * mm});
            skLineSegment(sketch, "E538", {"start": v(29.07, 5.22) * mm, "end": v(29.12, 5.54) * mm});
            skLineSegment(sketch, "E539", {"start": v(29.12, 5.54) * mm, "end": v(29.14, 5.7) * mm});
            skLineSegment(sketch, "E540", {"start": v(29.14, 5.7) * mm, "end": v(29.15, 5.77) * mm});
            skLineSegment(sketch, "E541", {"start": v(29.15, 5.77) * mm, "end": v(29.17, 5.84) * mm});
            skLineSegment(sketch, "E542", {"start": v(29.17, 5.84) * mm, "end": v(29.18, 5.91) * mm});
            skLineSegment(sketch, "E543", {"start": v(29.18, 5.91) * mm, "end": v(29.2, 5.98) * mm});
            skLineSegment(sketch, "E544", {"start": v(29.2, 5.98) * mm, "end": v(29.2, 6.04) * mm});
            skLineSegment(sketch, "E545", {"start": v(29.2, 6.04) * mm, "end": v(29.21, 6.1) * mm});
            skLineSegment(sketch, "E546", {"start": v(29.21, 6.1) * mm, "end": v(29.23, 6.16) * mm});
            skLineSegment(sketch, "E547", {"start": v(29.23, 6.16) * mm, "end": v(29.24, 6.2) * mm});
            skLineSegment(sketch, "E548", {"start": v(29.24, 6.2) * mm, "end": v(29.81, 9.5) * mm});
            skLineSegment(sketch, "E549", {"start": v(29.81, 9.5) * mm, "end": v(27.74, 9.82) * mm});
            skLineSegment(sketch, "E550", {"start": v(27.74, 9.82) * mm, "end": v(27.85, 10.42) * mm});
            skLineSegment(sketch, "E551", {"start": v(27.85, 10.42) * mm, "end": v(32.21, 10.42) * mm});
            skLineSegment(sketch, "E552", {"start": v(32.21, 10.42) * mm, "end": v(28.98, -7.77) * mm});
            skLineSegment(sketch, "E553", {"start": v(28.98, -7.77) * mm, "end": v(30.5, -8.1) * mm});
            skLineSegment(sketch, "E554", {"start": v(30.5, -8.1) * mm, "end": v(30.4, -8.7) * mm});
            skLineSegment(sketch, "E555", {"start": v(30.4, -8.7) * mm, "end": v(26.56, -8.7) * mm});
            skLineSegment(sketch, "E556", {"start": v(26.56, -8.7) * mm, "end": v(26.95, -6.6) * mm});
            skLineSegment(sketch, "E557", {"start": v(26.95, -6.6) * mm, "end": v(26.67, -6.9) * mm});
            skLineSegment(sketch, "E558", {"start": v(26.67, -6.9) * mm, "end": v(26.39, -7.16) * mm});
            skLineSegment(sketch, "E559", {"start": v(26.39, -7.16) * mm, "end": v(26.11, -7.42) * mm});
            skLineSegment(sketch, "E560", {"start": v(26.11, -7.42) * mm, "end": v(25.84, -7.65) * mm});
            skLineSegment(sketch, "E561", {"start": v(25.84, -7.65) * mm, "end": v(25.57, -7.86) * mm});
            skLineSegment(sketch, "E562", {"start": v(25.57, -7.86) * mm, "end": v(25.3, -8.06) * mm});
            skLineSegment(sketch, "E563", {"start": v(25.3, -8.06) * mm, "end": v(25.04, -8.24) * mm});
            skLineSegment(sketch, "E564", {"start": v(25.04, -8.24) * mm, "end": v(24.78, -8.4) * mm});
            skLineSegment(sketch, "E565", {"start": v(24.78, -8.4) * mm, "end": v(24.52, -8.54) * mm});
            skLineSegment(sketch, "E566", {"start": v(24.52, -8.54) * mm, "end": v(24.27, -8.66) * mm});
            skLineSegment(sketch, "E567", {"start": v(24.27, -8.66) * mm, "end": v(24.01, -8.76) * mm});
            skLineSegment(sketch, "E568", {"start": v(24.01, -8.76) * mm, "end": v(23.76, -8.84) * mm});
            skLineSegment(sketch, "E569", {"start": v(23.76, -8.84) * mm, "end": v(23.51, -8.9) * mm});
            skLineSegment(sketch, "E570", {"start": v(23.51, -8.9) * mm, "end": v(23.27, -8.95) * mm});
            skLineSegment(sketch, "E571", {"start": v(23.27, -8.95) * mm, "end": v(23.03, -8.98) * mm});
            skLineSegment(sketch, "E572", {"start": v(23.03, -8.98) * mm, "end": v(22.79, -9) * mm});
            skLineSegment(sketch, "E573", {"start": v(22.79, -9) * mm, "end": v(22.59, -8.99) * mm});
            skLineSegment(sketch, "E574", {"start": v(22.59, -8.99) * mm, "end": v(22.4, -8.97) * mm});
            skLineSegment(sketch, "E575", {"start": v(22.4, -8.97) * mm, "end": v(22.2, -8.95) * mm});
            skLineSegment(sketch, "E576", {"start": v(22.2, -8.95) * mm, "end": v(22.02, -8.91) * mm});
            skLineSegment(sketch, "E577", {"start": v(22.02, -8.91) * mm, "end": v(21.83, -8.87) * mm});
            skLineSegment(sketch, "E578", {"start": v(21.83, -8.87) * mm, "end": v(21.66, -8.82) * mm});
            skLineSegment(sketch, "E579", {"start": v(21.66, -8.82) * mm, "end": v(21.49, -8.75) * mm});
            skLineSegment(sketch, "E580", {"start": v(21.49, -8.75) * mm, "end": v(21.32, -8.68) * mm});
            skLineSegment(sketch, "E581", {"start": v(21.32, -8.68) * mm, "end": v(21.16, -8.6) * mm});
            skLineSegment(sketch, "E582", {"start": v(21.16, -8.6) * mm, "end": v(21, -8.5) * mm});
            skLineSegment(sketch, "E583", {"start": v(21, -8.5) * mm, "end": v(20.85, -8.41) * mm});
            skLineSegment(sketch, "E584", {"start": v(20.85, -8.41) * mm, "end": v(20.7, -8.3) * mm});
            skLineSegment(sketch, "E585", {"start": v(20.7, -8.3) * mm, "end": v(20.57, -8.19) * mm});
            skLineSegment(sketch, "E586", {"start": v(20.57, -8.19) * mm, "end": v(20.44, -8.07) * mm});
            skLineSegment(sketch, "E587", {"start": v(20.44, -8.07) * mm, "end": v(20.3, -7.93) * mm});
            skLineSegment(sketch, "E588", {"start": v(20.3, -7.93) * mm, "end": v(20.19, -7.8) * mm});
            skLineSegment(sketch, "E589", {"start": v(20.19, -7.8) * mm, "end": v(20.07, -7.64) * mm});
            skLineSegment(sketch, "E590", {"start": v(20.07, -7.64) * mm, "end": v(19.97, -7.48) * mm});
            skLineSegment(sketch, "E591", {"start": v(19.97, -7.48) * mm, "end": v(19.86, -7.31) * mm});
            skLineSegment(sketch, "E592", {"start": v(19.86, -7.31) * mm, "end": v(19.77, -7.14) * mm});
            skLineSegment(sketch, "E593", {"start": v(19.77, -7.14) * mm, "end": v(19.68, -6.95) * mm});
            skLineSegment(sketch, "E594", {"start": v(19.68, -6.95) * mm, "end": v(19.6, -6.76) * mm});
            skLineSegment(sketch, "E595", {"start": v(19.6, -6.76) * mm, "end": v(19.52, -6.56) * mm});
            skLineSegment(sketch, "E596", {"start": v(19.52, -6.56) * mm, "end": v(19.45, -6.35) * mm});
            skLineSegment(sketch, "E597", {"start": v(19.45, -6.35) * mm, "end": v(19.39, -6.14) * mm});
            skLineSegment(sketch, "E598", {"start": v(19.39, -6.14) * mm, "end": v(19.34, -5.91) * mm});
            skLineSegment(sketch, "E599", {"start": v(19.34, -5.91) * mm, "end": v(19.3, -5.69) * mm});
            skLineSegment(sketch, "E600", {"start": v(19.3, -5.69) * mm, "end": v(19.23, -5.2) * mm});
            skLineSegment(sketch, "E601", {"start": v(19.23, -5.2) * mm, "end": v(19.2, -4.7) * mm});
            skLineSegment(sketch, "E602", {"start": v(19.2, -4.7) * mm, "end": v(19.2, -4.44) * mm});
            skLineSegment(sketch, "E603", {"start": v(19.2, -4.44) * mm, "end": v(19.2, -3.87) * mm});
            skLineSegment(sketch, "E604", {"start": v(19.2, -3.87) * mm, "end": v(19.26, -3.3) * mm});
            skLineSegment(sketch, "E605", {"start": v(19.26, -3.3) * mm, "end": v(19.34, -2.74) * mm});
            skLineSegment(sketch, "E606", {"start": v(19.34, -2.74) * mm, "end": v(19.45, -2.2) * mm});
            skLineSegment(sketch, "E607", {"start": v(19.45, -2.2) * mm, "end": v(19.59, -1.65) * mm});
            skLineSegment(sketch, "E608", {"start": v(19.59, -1.65) * mm, "end": v(19.76, -1.12) * mm});
            skLineSegment(sketch, "E609", {"start": v(19.76, -1.12) * mm, "end": v(19.95, -0.61) * mm});
            skLineSegment(sketch, "E610", {"start": v(19.95, -0.61) * mm, "end": v(20.18, -0.12) * mm});
            skLineSegment(sketch, "E611", {"start": v(20.18, -0.12) * mm, "end": v(20.42, 0.35) * mm});
            skLineSegment(sketch, "E612", {"start": v(20.42, 0.35) * mm, "end": v(20.7, 0.8) * mm});
            skLineSegment(sketch, "E613", {"start": v(20.7, 0.8) * mm, "end": v(20.99, 1.24) * mm});
            skLineSegment(sketch, "E614", {"start": v(20.99, 1.24) * mm, "end": v(21.3, 1.64) * mm});
            skLineSegment(sketch, "E615", {"start": v(21.3, 1.64) * mm, "end": v(21.65, 2.03) * mm});
            skLineSegment(sketch, "E616", {"start": v(21.65, 2.03) * mm, "end": v(22.02, 2.4) * mm});
            skLineSegment(sketch, "E617", {"start": v(22.02, 2.4) * mm, "end": v(22.4, 2.73) * mm});
            skLineSegment(sketch, "E618", {"start": v(22.4, 2.73) * mm, "end": v(22.81, 3.03) * mm});
            skLineSegment(sketch, "E619", {"start": v(22.81, 3.03) * mm, "end": v(23.24, 3.31) * mm});
            skLineSegment(sketch, "E620", {"start": v(23.24, 3.31) * mm, "end": v(23.68, 3.56) * mm});
            skLineSegment(sketch, "E621", {"start": v(23.68, 3.56) * mm, "end": v(24.14, 3.77) * mm});
            skLineSegment(sketch, "E622", {"start": v(24.14, 3.77) * mm, "end": v(24.62, 3.95) * mm});
            skLineSegment(sketch, "E623", {"start": v(24.62, 3.95) * mm, "end": v(25.11, 4.09) * mm});
            skLineSegment(sketch, "E624", {"start": v(25.11, 4.09) * mm, "end": v(25.62, 4.19) * mm});
            skLineSegment(sketch, "E625", {"start": v(25.62, 4.19) * mm, "end": v(26.14, 4.25) * mm});
            skLineSegment(sketch, "E626", {"start": v(26.14, 4.25) * mm, "end": v(26.68, 4.27) * mm});
            skLineSegment(sketch, "E627", {"start": v(26.68, 4.27) * mm, "end": v(27, 4.26) * mm});
            skLineSegment(sketch, "E628", {"start": v(27, 4.26) * mm, "end": v(27.32, 4.25) * mm});
            skLineSegment(sketch, "E629", {"start": v(27.32, 4.25) * mm, "end": v(27.61, 4.22) * mm});
            skLineSegment(sketch, "E630", {"start": v(27.61, 4.22) * mm, "end": v(27.89, 4.19) * mm});
            skLineSegment(sketch, "E631", {"start": v(27.89, 4.19) * mm, "end": v(28.16, 4.14) * mm});
            skLineSegment(sketch, "E632", {"start": v(28.16, 4.14) * mm, "end": v(28.42, 4.1) * mm});
            skLineSegment(sketch, "E633", {"start": v(28.42, 4.1) * mm, "end": v(28.66, 4.03) * mm});
            skLineSegment(sketch, "E634", {"start": v(28.66, 4.03) * mm, "end": v(28.9, 3.96) * mm});
            skLineSegment(sketch, "E635", {"start": v(28.59, 2.56) * mm, "end": v(28.35, 2.7) * mm});
            skLineSegment(sketch, "E636", {"start": v(28.35, 2.7) * mm, "end": v(28.11, 2.84) * mm});
            skLineSegment(sketch, "E637", {"start": v(28.11, 2.84) * mm, "end": v(27.87, 2.95) * mm});
            skLineSegment(sketch, "E638", {"start": v(27.87, 2.95) * mm, "end": v(27.62, 3.04) * mm});
            skLineSegment(sketch, "E639", {"start": v(27.62, 3.04) * mm, "end": v(27.5, 3.09) * mm});
            skLineSegment(sketch, "E640", {"start": v(27.5, 3.09) * mm, "end": v(27.36, 3.12) * mm});
            skLineSegment(sketch, "E641", {"start": v(27.36, 3.12) * mm, "end": v(27.22, 3.15) * mm});
            skLineSegment(sketch, "E642", {"start": v(27.22, 3.15) * mm, "end": v(27.07, 3.18) * mm});
            skLineSegment(sketch, "E643", {"start": v(27.07, 3.18) * mm, "end": v(26.91, 3.2) * mm});
            skLineSegment(sketch, "E644", {"start": v(26.91, 3.2) * mm, "end": v(26.75, 3.2) * mm});
            skLineSegment(sketch, "E645", {"start": v(26.75, 3.2) * mm, "end": v(26.58, 3.22) * mm});
            skLineSegment(sketch, "E646", {"start": v(26.58, 3.22) * mm, "end": v(26.4, 3.22) * mm});
            skLineSegment(sketch, "E647", {"start": v(26.4, 3.22) * mm, "end": v(26.23, 3.21) * mm});
            skLineSegment(sketch, "E648", {"start": v(26.23, 3.21) * mm, "end": v(26.05, 3.2) * mm});
            skLineSegment(sketch, "E649", {"start": v(26.05, 3.2) * mm, "end": v(25.88, 3.18) * mm});
            skLineSegment(sketch, "E650", {"start": v(25.88, 3.18) * mm, "end": v(25.7, 3.14) * mm});
            skLineSegment(sketch, "E651", {"start": v(25.7, 3.14) * mm, "end": v(25.54, 3.1) * mm});
            skLineSegment(sketch, "E652", {"start": v(25.54, 3.1) * mm, "end": v(25.37, 3.05) * mm});
            skLineSegment(sketch, "E653", {"start": v(25.37, 3.05) * mm, "end": v(25.2, 2.98) * mm});
            skLineSegment(sketch, "E654", {"start": v(25.2, 2.98) * mm, "end": v(25.05, 2.91) * mm});
            skLineSegment(sketch, "E655", {"start": v(25.05, 2.91) * mm, "end": v(24.9, 2.83) * mm});
            skLineSegment(sketch, "E656", {"start": v(24.9, 2.83) * mm, "end": v(24.59, 2.65) * mm});
            skLineSegment(sketch, "E657", {"start": v(24.59, 2.65) * mm, "end": v(24.3, 2.43) * mm});
            skLineSegment(sketch, "E658", {"start": v(24.3, 2.43) * mm, "end": v(24.01, 2.2) * mm});
            skLineSegment(sketch, "E659", {"start": v(24.01, 2.2) * mm, "end": v(23.88, 2.06) * mm});
            skLineSegment(sketch, "E660", {"start": v(23.88, 2.06) * mm, "end": v(23.61, 1.79) * mm});
            skLineSegment(sketch, "E661", {"start": v(23.61, 1.79) * mm, "end": v(23.37, 1.49) * mm});
            skLineSegment(sketch, "E662", {"start": v(23.37, 1.49) * mm, "end": v(23.13, 1.17) * mm});
            skLineSegment(sketch, "E663", {"start": v(23.13, 1.17) * mm, "end": v(22.9, 0.82) * mm});
            skLineSegment(sketch, "E664", {"start": v(22.9, 0.82) * mm, "end": v(22.7, 0.46) * mm});
            skLineSegment(sketch, "E665", {"start": v(22.7, 0.46) * mm, "end": v(22.52, 0.08) * mm});
            skLineSegment(sketch, "E666", {"start": v(22.52, 0.08) * mm, "end": v(22.35, -0.3) * mm});
            skLineSegment(sketch, "E667", {"start": v(22.35, -0.3) * mm, "end": v(22.2, -0.71) * mm});
            skLineSegment(sketch, "E668", {"start": v(22.2, -0.71) * mm, "end": v(22.05, -1.13) * mm});
            skLineSegment(sketch, "E669", {"start": v(22.05, -1.13) * mm, "end": v(21.83, -1.97) * mm});
            skLineSegment(sketch, "E670", {"start": v(21.83, -1.97) * mm, "end": v(21.74, -2.4) * mm});
            skLineSegment(sketch, "E671", {"start": v(21.74, -2.4) * mm, "end": v(21.67, -2.84) * mm});
            skLineSegment(sketch, "E672", {"start": v(21.67, -2.84) * mm, "end": v(21.6, -3.71) * mm});
            skLineSegment(sketch, "E673", {"start": v(21.6, -3.71) * mm, "end": v(21.59, -4.14) * mm});
            skLineSegment(sketch, "E674", {"start": v(21.59, -4.14) * mm, "end": v(21.6, -4.35) * mm});
            skLineSegment(sketch, "E675", {"start": v(21.6, -4.35) * mm, "end": v(21.6, -4.55) * mm});
            skLineSegment(sketch, "E676", {"start": v(21.6, -4.55) * mm, "end": v(21.62, -4.75) * mm});
            skLineSegment(sketch, "E677", {"start": v(21.62, -4.75) * mm, "end": v(21.64, -4.93) * mm});
            skLineSegment(sketch, "E678", {"start": v(21.64, -4.93) * mm, "end": v(21.66, -5.1) * mm});
            skLineSegment(sketch, "E679", {"start": v(21.66, -5.1) * mm, "end": v(21.7, -5.28) * mm});
            skLineSegment(sketch, "E680", {"start": v(21.7, -5.28) * mm, "end": v(21.73, -5.44) * mm});
            skLineSegment(sketch, "E681", {"start": v(21.73, -5.44) * mm, "end": v(21.78, -5.6) * mm});
            skLineSegment(sketch, "E682", {"start": v(21.78, -5.6) * mm, "end": v(21.83, -5.74) * mm});
            skLineSegment(sketch, "E683", {"start": v(21.83, -5.74) * mm, "end": v(21.88, -5.88) * mm});
            skLineSegment(sketch, "E684", {"start": v(21.88, -5.88) * mm, "end": v(21.93, -6.01) * mm});
            skLineSegment(sketch, "E685", {"start": v(21.93, -6.01) * mm, "end": v(22, -6.14) * mm});
            skLineSegment(sketch, "E686", {"start": v(22, -6.14) * mm, "end": v(22.05, -6.26) * mm});
            skLineSegment(sketch, "E687", {"start": v(22.05, -6.26) * mm, "end": v(22.12, -6.37) * mm});
            skLineSegment(sketch, "E688", {"start": v(22.12, -6.37) * mm, "end": v(22.19, -6.48) * mm});
            skLineSegment(sketch, "E689", {"start": v(22.19, -6.48) * mm, "end": v(22.26, -6.58) * mm});
            skLineSegment(sketch, "E690", {"start": v(22.26, -6.58) * mm, "end": v(22.34, -6.67) * mm});
            skLineSegment(sketch, "E691", {"start": v(22.34, -6.67) * mm, "end": v(22.42, -6.76) * mm});
            skLineSegment(sketch, "E692", {"start": v(22.42, -6.76) * mm, "end": v(22.5, -6.84) * mm});
            skLineSegment(sketch, "E693", {"start": v(22.5, -6.84) * mm, "end": v(22.6, -6.9) * mm});
            skLineSegment(sketch, "E694", {"start": v(22.6, -6.9) * mm, "end": v(22.68, -6.97) * mm});
            skLineSegment(sketch, "E695", {"start": v(22.68, -6.97) * mm, "end": v(22.77, -7.03) * mm});
            skLineSegment(sketch, "E696", {"start": v(22.77, -7.03) * mm, "end": v(22.87, -7.09) * mm});
            skLineSegment(sketch, "E697", {"start": v(22.87, -7.09) * mm, "end": v(22.96, -7.13) * mm});
            skLineSegment(sketch, "E698", {"start": v(22.96, -7.13) * mm, "end": v(23.06, -7.17) * mm});
            skLineSegment(sketch, "E699", {"start": v(23.06, -7.17) * mm, "end": v(23.16, -7.2) * mm});
            skLineSegment(sketch, "E700", {"start": v(23.16, -7.2) * mm, "end": v(23.27, -7.24) * mm});
            skLineSegment(sketch, "E701", {"start": v(23.27, -7.24) * mm, "end": v(23.37, -7.26) * mm});
            skLineSegment(sketch, "E702", {"start": v(23.37, -7.26) * mm, "end": v(23.47, -7.28) * mm});
            skLineSegment(sketch, "E703", {"start": v(23.47, -7.28) * mm, "end": v(23.58, -7.3) * mm});
            skLineSegment(sketch, "E704", {"start": v(23.58, -7.3) * mm, "end": v(23.68, -7.3) * mm});
            skLineSegment(sketch, "E705", {"start": v(23.68, -7.3) * mm, "end": v(23.78, -7.3) * mm});
            skLineSegment(sketch, "E706", {"start": v(23.78, -7.3) * mm, "end": v(23.97, -7.3) * mm});
            skLineSegment(sketch, "E707", {"start": v(23.97, -7.3) * mm, "end": v(24.17, -7.28) * mm});
            skLineSegment(sketch, "E708", {"start": v(24.17, -7.28) * mm, "end": v(24.37, -7.24) * mm});
            skLineSegment(sketch, "E709", {"start": v(24.37, -7.24) * mm, "end": v(24.57, -7.19) * mm});
            skLineSegment(sketch, "E710", {"start": v(24.57, -7.19) * mm, "end": v(24.77, -7.12) * mm});
            skLineSegment(sketch, "E711", {"start": v(24.77, -7.12) * mm, "end": v(24.98, -7.04) * mm});
            skLineSegment(sketch, "E712", {"start": v(24.98, -7.04) * mm, "end": v(25.2, -6.94) * mm});
            skLineSegment(sketch, "E713", {"start": v(25.2, -6.94) * mm, "end": v(25.41, -6.82) * mm});
            skLineSegment(sketch, "E714", {"start": v(25.41, -6.82) * mm, "end": v(25.63, -6.7) * mm});
            skLineSegment(sketch, "E715", {"start": v(25.63, -6.7) * mm, "end": v(25.85, -6.55) * mm});
            skLineSegment(sketch, "E716", {"start": v(25.85, -6.55) * mm, "end": v(26.07, -6.4) * mm});
            skLineSegment(sketch, "E717", {"start": v(26.07, -6.4) * mm, "end": v(26.28, -6.23) * mm});
            skLineSegment(sketch, "E718", {"start": v(26.28, -6.23) * mm, "end": v(26.5, -6.05) * mm});
            skLineSegment(sketch, "E719", {"start": v(26.5, -6.05) * mm, "end": v(26.92, -5.65) * mm});
            skLineSegment(sketch, "E720", {"start": v(26.92, -5.65) * mm, "end": v(27.12, -5.44) * mm});
            skLineSegment(sketch, "E721", {"start": v(27.12, -5.44) * mm, "end": v(28.59, 2.56) * mm});
            skSolve(sketch);
        }
        {
            var Q0;
            Q0=makeQuery(id+"F0.imprint","IMPRINT",FACE,{"disambiguationData":[TD([[makeQuery(id+"F0.imprint","IMPRINT",EDGE,{"derivedFrom":sQuery(id+"F0.wireOp",EDGE,"9c274906-66f2-47cc-ba81-bc829715841a")}),-1.0]])]});
            var Q1;
            {var subQ1=sQuery(id+"F0.wireOp",EDGE,"E3");Q1=makeQuery(id+"F0.imprint","IMPRINT",FACE,{"disambiguationData":[TD([[makeQuery(id+"F0.imprint","IMPRINT",EDGE,{"derivedFrom":subQ1}),-1.0]])]});}
            var Q2;
            Q2=makeQuery(id+"F0.imprint","IMPRINT",FACE,{"disambiguationData":[TD([[makeQuery(id+"F0.imprint","IMPRINT",EDGE,{"derivedFrom":sQuery(id+"F0.wireOp",EDGE,"6ab65d4b-20cc-4260-84e2-1f812e6f8199")}),1.0]])]});
            var Q3;
            Q3=makeQuery(id+"F0.imprint","IMPRINT",FACE,{"disambiguationData":[TD([[makeQuery(id+"F0.imprint","IMPRINT",EDGE,{"derivedFrom":sQuery(id+"F0.wireOp",EDGE,"fbc92326-29e4-4a65-8bcc-6a279c66f74b")}),-1.0]])]});
            var Q4;
            Q4=makeQuery(id+"F0.imprint","IMPRINT",FACE,{"disambiguationData":[TD([[makeQuery(id+"F0.imprint","IMPRINT",EDGE,{"derivedFrom":sQuery(id+"F0.wireOp",EDGE,"E1")}),1.0]])]});
            var Q5;
            Q5=makeQuery(id+"F0.imprint","IMPRINT",FACE,{"disambiguationData":[TD([[makeQuery(id+"F0.imprint","IMPRINT",EDGE,{"derivedFrom":sQuery(id+"F0.wireOp",EDGE,"edff43eb-599a-4c31-8809-e4d85603c349")}),-1.0]])]});
            var Q6;
            Q6=makeQuery(id+"F0.imprint","IMPRINT",FACE,{"disambiguationData":[TD([[makeQuery(id+"F0.imprint","IMPRINT",EDGE,{"derivedFrom":sQuery(id+"F0.wireOp",EDGE,"9c1aa12f-a708-4583-be26-2b383a722471")}),1.0]])]});
            var Q7;
            Q7=makeQuery(id+"F0.imprint","IMPRINT",FACE,{"disambiguationData":[TD([[makeQuery(id+"F0.imprint","IMPRINT",EDGE,{"derivedFrom":sQuery(id+"F0.wireOp",EDGE,"d64aa239-00f7-4386-9746-6503c5a989f5")}),-1.0]])]});
            var Q8;
            {var subQ5=sQuery(id+"F0.wireOp",EDGE,"a99f0830-5d0a-4233-9662-b7695eaebfe7");Q8=makeQuery(id+"F0.imprint","IMPRINT",FACE,{"disambiguationData":[TD([[makeQuery(id+"F0.imprint","IMPRINT",EDGE,{"derivedFrom":subQ5}),-1.0]])]});}
            var Q9;
            Q9=makeQuery(id+"F0.imprint","IMPRINT",FACE,{"disambiguationData":[TD([[makeQuery(id+"F0.imprint","IMPRINT",EDGE,{"derivedFrom":sQuery(id+"F0.wireOp",EDGE,"2a4fbe35-dfba-4a85-95bd-e9da396d757a")}),-1.0]])]});
            var Q10;
            Q10=makeQuery(id+"F0.imprint","IMPRINT",FACE,{"disambiguationData":[TD([[makeQuery(id+"F0.imprint","IMPRINT",EDGE,{"derivedFrom":sQuery(id+"F0.wireOp",EDGE,"2a4fbe35-dfba-4a85-95bd-e9da396d757a")}),1.0]])]});
            var Q11;
            Q11=makeQuery(id+"F0.imprint","IMPRINT",FACE,{"disambiguationData":[TD([[makeQuery(id+"F0.imprint","IMPRINT",EDGE,{"derivedFrom":sQuery(id+"F0.wireOp",EDGE,"7aec7717-0c6f-4bae-bb6d-1404d206293c")}),-1.0]])]});
            var Q12;
            Q12=makeQuery(id+"F0.imprint","IMPRINT",FACE,{"disambiguationData":[TD([[makeQuery(id+"F0.imprint","IMPRINT",EDGE,{"derivedFrom":sQuery(id+"F0.wireOp",EDGE,"2e831668-c073-46cd-8cf9-afdbba8640c2")}),-1.0]])]});
            var Q13;
            Q13=makeQuery(id+"F0.imprint","IMPRINT",FACE,{"disambiguationData":[TD([[makeQuery(id+"F0.imprint","IMPRINT",EDGE,{"derivedFrom":sQuery(id+"F0.wireOp",EDGE,"0ff61a9d-bce7-4498-a74a-3b659cdb3a31")}),1.0]])]});
            var Q14;
            Q14=makeQuery(id+"F0.imprint","IMPRINT",FACE,{"disambiguationData":[TD([[makeQuery(id+"F0.imprint","IMPRINT",EDGE,{"derivedFrom":sQuery(id+"F0.wireOp",EDGE,"a042b107-2d44-4470-895e-1f3e02275d71")}),-1.0]])]});
            var Q15;
            Q15=makeQuery(id+"F0.imprint","IMPRINT",FACE,{"disambiguationData":[TD([[makeQuery(id+"F0.imprint","IMPRINT",EDGE,{"derivedFrom":sQuery(id+"F0.wireOp",EDGE,"95c83fbc-b161-4fb0-9650-2e0c3f26e526")}),-1.0]])]});
            var Q16;
            Q16=makeQuery(id+"F0.imprint","IMPRINT",FACE,{"disambiguationData":[TD([[makeQuery(id+"F0.imprint","IMPRINT",EDGE,{"derivedFrom":sQuery(id+"F0.wireOp",EDGE,"b99bc01f-ffcd-4b76-b182-fcdfcf3af48a")}),-1.0]])]});
            var Q17;
            Q17=makeQuery(id+"F0.imprint","IMPRINT",FACE,{"disambiguationData":[TD([[makeQuery(id+"F0.imprint","IMPRINT",EDGE,{"derivedFrom":sQuery(id+"F0.wireOp",EDGE,"695980f6-fe78-45aa-8406-9730c21c461c")}),-1.0]])]});
            var Q18;
            Q18=makeQuery(id+"F0.imprint","IMPRINT",FACE,{"disambiguationData":[TD([[makeQuery(id+"F0.imprint","IMPRINT",EDGE,{"derivedFrom":sQuery(id+"F0.wireOp",EDGE,"8e396e48-0cb7-43f7-9ff5-ea5343fde688")}),-1.0]])]});
            var Q19;
            Q19=makeQuery(id+"F0.imprint","IMPRINT",FACE,{"disambiguationData":[TD([[makeQuery(id+"F0.imprint","IMPRINT",EDGE,{"derivedFrom":sQuery(id+"F0.wireOp",EDGE,"f8601505-93ae-4942-8ee9-6dae2b73583f")}),-1.0]])]});
            var Q20;
            Q20=makeQuery(id+"F0.imprint","IMPRINT",FACE,{"disambiguationData":[TD([[makeQuery(id+"F0.imprint","IMPRINT",EDGE,{"derivedFrom":sQuery(id+"F0.wireOp",EDGE,"328a7c4d-a5ec-4a4b-9363-a6ff0bef3fca")}),1.0]])]});
            var Q21;
            Q21=makeQuery(id+"F0.imprint","IMPRINT",FACE,{"disambiguationData":[TD([[makeQuery(id+"F0.imprint","IMPRINT",EDGE,{"derivedFrom":sQuery(id+"F0.wireOp",EDGE,"1e94215b-109c-49a7-b724-ba8efd773434")}),1.0]])]});
            var Q22;
            Q22=makeQuery(id+"F0.imprint","IMPRINT",FACE,{"disambiguationData":[TD([[makeQuery(id+"F0.imprint","IMPRINT",EDGE,{"derivedFrom":sQuery(id+"F0.wireOp",EDGE,"21f35bfe-fe16-479b-9939-4457bf5feded")}),-1.0]])]});
            var Q23;
            Q23=makeQuery(id+"F0.imprint","IMPRINT",FACE,{"disambiguationData":[TD([[makeQuery(id+"F0.imprint","IMPRINT",EDGE,{"derivedFrom":sQuery(id+"F0.wireOp",EDGE,"e0ee4744-029e-4183-8adc-bc2568514006")}),-1.0]])]});
            var Q24;
            Q24=makeQuery(id+"F0.imprint","IMPRINT",FACE,{"disambiguationData":[TD([[makeQuery(id+"F0.imprint","IMPRINT",EDGE,{"derivedFrom":sQuery(id+"F0.wireOp",EDGE,"84324da4-f598-4ddc-853e-288e39188647")}),-1.0]])]});
            var Q25;
            Q25=makeQuery(id+"F0.imprint","IMPRINT",FACE,{"disambiguationData":[TD([[makeQuery(id+"F0.imprint","IMPRINT",EDGE,{"derivedFrom":sQuery(id+"F0.wireOp",EDGE,"712d350e-d0bc-4a1d-9dcc-c594a14d8721")}),-1.0]])]});
            var Q26;
            Q26=makeQuery(id+"F0.imprint","IMPRINT",FACE,{"disambiguationData":[TD([[makeQuery(id+"F0.imprint","IMPRINT",EDGE,{"derivedFrom":sQuery(id+"F0.wireOp",EDGE,"b0387f20-0e19-48e0-a450-f759074d4cab")}),1.0]])]});
            var Q27;
            Q27=makeQuery(id+"F0.imprint","IMPRINT",FACE,{"disambiguationData":[TD([[makeQuery(id+"F0.imprint","IMPRINT",EDGE,{"derivedFrom":sQuery(id+"F0.wireOp",EDGE,"136f4ab2-2075-402f-bfa0-9a1a10c9402b")}),-1.0]])]});
            var Q28;
            Q28=makeQuery(id+"F0.imprint","IMPRINT",FACE,{"disambiguationData":[TD([[makeQuery(id+"F0.imprint","IMPRINT",EDGE,{"derivedFrom":sQuery(id+"F0.wireOp",EDGE,"82aa7b26-31b1-4185-969d-2b6ef5c613a2")}),-1.0]])]});
            var Q29;
            Q29=makeQuery(id+"F0.imprint","IMPRINT",FACE,{"disambiguationData":[TD([[makeQuery(id+"F0.imprint","IMPRINT",EDGE,{"derivedFrom":sQuery(id+"F0.wireOp",EDGE,"dbadadc4-0d52-4bda-b846-840137564e02")}),-1.0]])]});
            var Q30;
            Q30=makeQuery(id+"F0.imprint","IMPRINT",FACE,{"disambiguationData":[TD([[makeQuery(id+"F0.imprint","IMPRINT",EDGE,{"derivedFrom":sQuery(id+"F0.wireOp",EDGE,"2aa94a68-3a36-45ea-9fbc-5b17c4104d49")}),-1.0]])]});
            var Q31;
            Q31=makeQuery(id+"F0.imprint","IMPRINT",FACE,{"disambiguationData":[TD([[makeQuery(id+"F0.imprint","IMPRINT",EDGE,{"derivedFrom":sQuery(id+"F0.wireOp",EDGE,"00d53613-514a-4d13-8ea6-4e0a7ee6f204")}),1.0]])]});
            var Q32;
            Q32=makeQuery(id+"F0.imprint","IMPRINT",FACE,{"disambiguationData":[TD([[makeQuery(id+"F0.imprint","IMPRINT",EDGE,{"derivedFrom":sQuery(id+"F0.wireOp",EDGE,"E5")}),-1.0]])]});
            var Q33;
            Q33=makeQuery(id+"F0.imprint","IMPRINT",FACE,{"disambiguationData":[TD([[makeQuery(id+"F0.imprint","IMPRINT",EDGE,{"derivedFrom":sQuery(id+"F0.wireOp",EDGE,"E31")}),-1.0]])]});
            var Q34;
            Q34=makeQuery(id+"F0.imprint","IMPRINT",FACE,{"disambiguationData":[TD([[makeQuery(id+"F0.imprint","IMPRINT",EDGE,{"derivedFrom":sQuery(id+"F0.wireOp",EDGE,"E248")}),-1.0]])]});
            var Q35;
            Q35=makeQuery(id+"F0.imprint","IMPRINT",FACE,{"disambiguationData":[TD([[makeQuery(id+"F0.imprint","IMPRINT",EDGE,{"derivedFrom":sQuery(id+"F0.wireOp",EDGE,"E433")}),1.0]])]});
            var Q36;
            Q36=makeQuery(id+"F0.imprint","IMPRINT",FACE,{"disambiguationData":[TD([[makeQuery(id+"F0.imprint","IMPRINT",EDGE,{"derivedFrom":sQuery(id+"F0.wireOp",EDGE,"E128")}),-1.0]])]});
            var Q37;
            Q37=makeQuery(id+"F0.imprint","IMPRINT",FACE,{"disambiguationData":[TD([[makeQuery(id+"F0.imprint","IMPRINT",EDGE,{"derivedFrom":sQuery(id+"F0.wireOp",EDGE,"E516")}),-1.0]])]});
            var Q38;
            Q38=makeQuery(id+"F0.imprint","IMPRINT",FACE,{"disambiguationData":[TD([[makeQuery(id+"F0.imprint","IMPRINT",EDGE,{"derivedFrom":sQuery(id+"F0.wireOp",EDGE,"E635")}),1.0]])]});
            var Q39;
            Q39=makeQuery(id+"F0.imprint","IMPRINT",FACE,{"disambiguationData":[TD([[makeQuery(id+"F0.imprint","IMPRINT",EDGE,{"derivedFrom":sQuery(id+"F0.wireOp",EDGE,"E524")}),-1.0]])]});
            extrude(context, id + "F1", {"entities" : qUnion([Q0, Q1, Q2, Q3, Q4, Q5, Q6, Q7, Q8, Q9, Q10, Q11, Q12, Q13, Q14, Q15, Q16, Q17, Q18, Q19, Q20, Q21, Q22, Q23, Q24, Q25, Q26, Q27, Q28, Q29, Q30, Q31, Q32, Q33, Q34, Q35, Q36, Q37, Q38, Q39]), "oppositeDirection" : true, "depth" : 1.6 * mm, "offsetDistance" : 25 * mm});
        }
        {
            var Q0;
            Q0=makeQuery(id+"F0.imprint","IMPRINT",FACE,{"disambiguationData":[TD([[makeQuery(id+"F0.imprint","IMPRINT",EDGE,{"derivedFrom":sQuery(id+"F0.wireOp",EDGE,"E1")}),1.0]])]});
            extrude(context, id + "F2", {"entities" : qUnion([Q0]), "operationType" : NewBodyOperationType.ADD, "depth" : 1.6 * mm, "offsetDistance" : 25 * mm});
        }
        {
            var Q0;
            Q0=makeQuery(id+"F0.imprint","IMPRINT",FACE,{"disambiguationData":[TD([[makeQuery(id+"F0.imprint","IMPRINT",EDGE,{"derivedFrom":sQuery(id+"F0.wireOp",EDGE,"E5")}),-1.0]])]});
            var Q1;
            Q1=makeQuery(id+"F0.imprint","IMPRINT",FACE,{"disambiguationData":[TD([[makeQuery(id+"F0.imprint","IMPRINT",EDGE,{"derivedFrom":sQuery(id+"F0.wireOp",EDGE,"E31")}),-1.0]])]});
            var Q2;
            Q2=makeQuery(id+"F0.imprint","IMPRINT",FACE,{"disambiguationData":[TD([[makeQuery(id+"F0.imprint","IMPRINT",EDGE,{"derivedFrom":sQuery(id+"F0.wireOp",EDGE,"E128")}),-1.0]])]});
            var Q3;
            Q3=makeQuery(id+"F0.imprint","IMPRINT",FACE,{"disambiguationData":[TD([[makeQuery(id+"F0.imprint","IMPRINT",EDGE,{"derivedFrom":sQuery(id+"F0.wireOp",EDGE,"E248")}),-1.0]])]});
            var Q4;
            Q4=makeQuery(id+"F0.imprint","IMPRINT",FACE,{"disambiguationData":[TD([[makeQuery(id+"F0.imprint","IMPRINT",EDGE,{"derivedFrom":sQuery(id+"F0.wireOp",EDGE,"E516")}),-1.0]])]});
            var Q5;
            Q5=makeQuery(id+"F0.imprint","IMPRINT",FACE,{"disambiguationData":[TD([[makeQuery(id+"F0.imprint","IMPRINT",EDGE,{"derivedFrom":sQuery(id+"F0.wireOp",EDGE,"E524")}),-1.0]])]});
            extrude(context, id + "F3", {"entities" : qUnion([Q0, Q1, Q2, Q3, Q4, Q5]), "operationType" : NewBodyOperationType.ADD, "depth" : 1.2 * mm, "offsetDistance" : 25 * mm});
        }
    });
